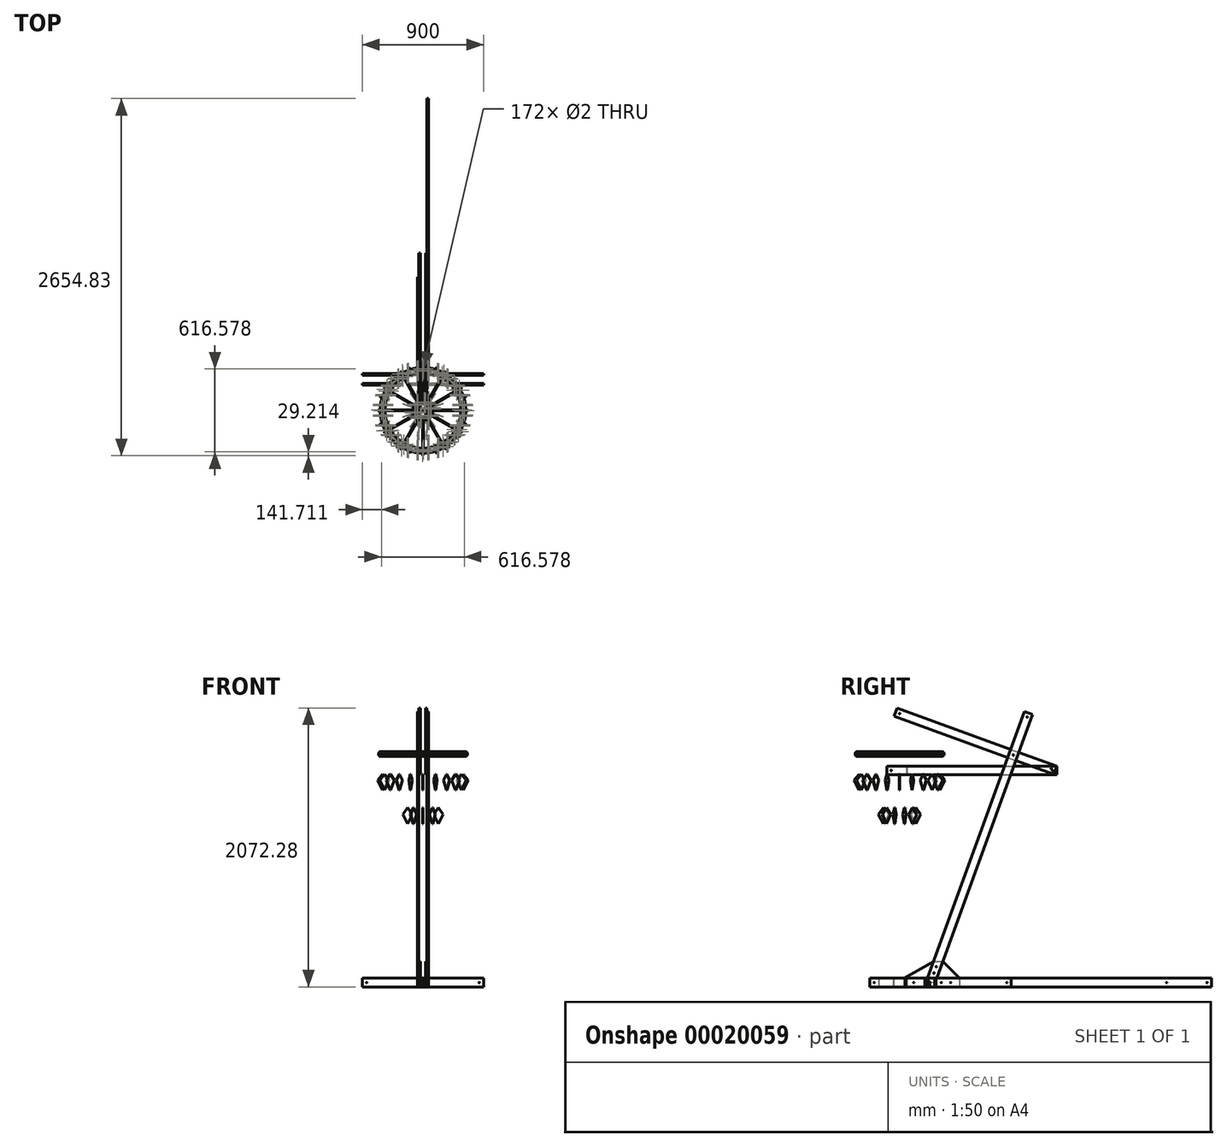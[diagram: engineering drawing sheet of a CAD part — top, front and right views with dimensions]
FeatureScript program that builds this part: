
annotation { "Feature Type Name" : "Feature", "Feature Type Description" : "" }
export const myFeature = defineFeature(function(context is Context, id is Id, definition is map)
    precondition{}
    {
        {
            var Q0;
            Q0=qCreatedBy(makeId("Right.planeOp"),FACE);
            var sketch = newSketch(context, id + "F0", { "sketchPlane" : qUnion([Q0])});
            skLineSegment(sketch, "E0", {"start": v(0, 0) * mm, "end": v(-450, 0) * mm});
            skLineSegment(sketch, "E1", {"start": v(0, 0) * mm, "end": v(600, 0) * mm});
            skLineSegment(sketch, "E2", {"start": v(0, 0) * mm, "end": v(615.64, 1691.45) * mm});
            skLineSegment(sketch, "E3", {"start": v(615.64, 1691.45) * mm, "end": v(718.24, 1973.35) * mm});
            skLineSegment(sketch, "E4", {"start": v(615.64, 1691.45) * mm, "end": v(897.54, 1588.84) * mm});
            skLineSegment(sketch, "E5", {"start": v(615.64, 1691.45) * mm, "end": v(-230.09, 1999.26) * mm});
            skLineSegment(sketch, "E6", {"start": v(-230.09, 1999.26) * mm, "end": v(-230.09, 1699.26) * mm});
            skLineSegment(sketch, "E7", {"start": v(-230.09, 1699.26) * mm, "end": v(-530.09, 1699.26) * mm});
            skLineSegment(sketch, "E8", {"start": v(-230.09, 1699.26) * mm, "end": v(69.91, 1699.26) * mm});
            skLineSegment(sketch, "E9", {"start": v(-530.09, 1699.26) * mm, "end": v(-530.09, 1399.26) * mm});
            skLineSegment(sketch, "E10", {"start": v(69.91, 1699.26) * mm, "end": v(69.91, 1399.26) * mm});
            skSolve(sketch);
        }
        {
            var Q0;
            Q0=qCreatedBy(makeId("Front.planeOp"),FACE);
            var sketch = newSketch(context, id + "F1", { "sketchPlane" : qUnion([Q0])});
            skLineSegment(sketch, "E11", {"start": v(0, 0) * mm, "end": v(450, 0) * mm});
            skLineSegment(sketch, "E12", {"start": v(0, 0) * mm, "end": v(-450, 0) * mm});
            skSolve(sketch);
        }
        {
            var Q0;
            Q0=qCreatedBy(makeId("Right.planeOp"),FACE);
            var sketch = newSketch(context, id + "F2", { "sketchPlane" : qUnion([Q0])});
            skLineSegment(sketch, "E13.0", {"start": v(-230.09, 1699.26) * mm, "end": v(69.91, 1699.26) * mm});
            skLineSegment(sketch, "E14", {"start": v(-230.09, 1693.26) * mm, "end": v(69.91, 1693.26) * mm});
            skLineSegment(sketch, "E15", {"start": v(69.91, 1693.26) * mm, "end": v(69.91, 1699.26) * mm});
            skLineSegment(sketch, "E16", {"start": v(-230.09, 1699.26) * mm, "end": v(-230.09, 1693.26) * mm});
            skSolve(sketch);
        }
        {
            var Q0;
            Q0=makeQuery(id+"F2.imprint","IMPRINT",FACE,{"disambiguationData":[TD([[makeQuery(id+"F2.imprint","IMPRINT",EDGE,{"derivedFrom":sQuery(id+"F2.wireOp",EDGE,"E13.0")}),-1.0]])]});
            var Q1;
            Q1=sQuery(id+"F0.wireOp",EDGE,"E6");
            revolve(context, id + "F3", {"entities" : qUnion([Q0]), "axis" : qUnion([Q1]), "revolveType" : RevolveType.FULL});
        }
        {
            var Q0;
            Q0=qCreatedBy(makeId("Right.planeOp"),FACE);
            var sketch = newSketch(context, id + "F4", { "sketchPlane" : qUnion([Q0])});
            skLineSegment(sketch, "E17", {"start": v(-450.4, 0) * mm, "end": v(-450.4, 32) * mm});
            skPoint(sketch, "E18.0", {"position": v(600, 0) * mm});
            skLineSegment(sketch, "E19", {"start": v(-450.4, 32) * mm, "end": v(-42, 32) * mm});
            skLineSegment(sketch, "E20", {"start": v(600, 32) * mm, "end": v(600, 0) * mm});
            skLineSegment(sketch, "E21", {"start": v(600, 0) * mm, "end": v(600, -32) * mm});
            skLineSegment(sketch, "E22", {"start": v(600, -32) * mm, "end": v(-450.4, -32) * mm});
            skLineSegment(sketch, "E23", {"start": v(-450.4, -32) * mm, "end": v(-450.4, 0) * mm});
            skLineSegment(sketch, "E24.top", {"start": v(-30, 0) * mm, "end": v(-42, 0) * mm});
            skLineSegment(sketch, "E24.left", {"start": v(-30, 32) * mm, "end": v(-30, 0) * mm});
            skLineSegment(sketch, "E24.right", {"start": v(-42, 32) * mm, "end": v(-42, 0) * mm});
            skLineSegment(sketch, "E25.top", {"start": v(30, 0) * mm, "end": v(42, 0) * mm});
            skLineSegment(sketch, "E25.left", {"start": v(30, 32) * mm, "end": v(30, 0) * mm});
            skLineSegment(sketch, "E25.right", {"start": v(42, 32) * mm, "end": v(42, 0) * mm});
            skLineSegment(sketch, "E26.trimOffspring", {"start": v(-30, 32) * mm, "end": v(30, 32) * mm});
            skLineSegment(sketch, "E27.trimOffspring", {"start": v(42, 32) * mm, "end": v(600, 32) * mm});
            skLineSegment(sketch, "E28", {"start": v(0, 0) * mm, "end": v(0, 32) * mm, "construction": true});
            skSolve(sketch);
        }
        {
            var Q0;
            Q0=makeQuery(id+"F4.imprint","IMPRINT",FACE,{"disambiguationData":[TD([[makeQuery(id+"F4.imprint","IMPRINT",EDGE,{"derivedFrom":sQuery(id+"F4.wireOp",EDGE,"E17")}),-1.0]])]});
            extrude(context, id + "F5", {"entities" : qUnion([Q0]), "depth" : 12 * mm});
        }
        {
            var Q0;
            Q0=makeQuery(id+"F5.opExtrude","SWEPT_BODY",BODY,{"disambiguationData":[OSD([sQuery(id+"F4.wireOp",EDGE,"E17"),sQuery(id+"F4.wireOp",EDGE,"E19"),sQuery(id+"F4.wireOp",EDGE,"E20"),sQuery(id+"F4.wireOp",EDGE,"E21"),sQuery(id+"F4.wireOp",EDGE,"E22"),sQuery(id+"F4.wireOp",EDGE,"E23")])]});
            var Q1;
            Q1=sQuery(id+"F1.wireOp",EDGE,"E11");
            transform(context, id + "F6", {"entities" : qUnion([Q0]), "transformType" : TransformType.TRANSLATION_DISTANCE, "transformDirection" : qUnion([Q1]), "distance" : (12 * 2.5) * mm, "makeCopy" : false});
        }
        {
            var Q0;
            Q0=makeQuery(id+"F5.opExtrude","SWEPT_BODY",BODY,{"disambiguationData":[OSD([sQuery(id+"F4.wireOp",EDGE,"E17"),sQuery(id+"F4.wireOp",EDGE,"E19"),sQuery(id+"F4.wireOp",EDGE,"E20"),sQuery(id+"F4.wireOp",EDGE,"E21"),sQuery(id+"F4.wireOp",EDGE,"E22"),sQuery(id+"F4.wireOp",EDGE,"E23")])]});
            var Q1;
            Q1=qCreatedBy(makeId("Right.planeOp"),FACE);
            mirror(context, id + "F7", {"entities" : qUnion([Q0]), "mirrorPlane" : qUnion([Q1])});
        }
        {
            var Q0;
            Q0=qCreatedBy(makeId("Front.planeOp"),FACE);
            var sketch = newSketch(context, id + "F8", { "sketchPlane" : qUnion([Q0])});
            skPoint(sketch, "E29.0", {"position": v(-450, 0) * mm});
            skPoint(sketch, "E30.0", {"position": v(450, 0) * mm});
            skLineSegment(sketch, "E31", {"start": v(-450, 0) * mm, "end": v(-450, 32) * mm});
            skLineSegment(sketch, "E32", {"start": v(450, 32) * mm, "end": v(450, 0) * mm});
            skLineSegment(sketch, "E33", {"start": v(450, 0) * mm, "end": v(450, -32) * mm});
            skLineSegment(sketch, "E34", {"start": v(450, -32) * mm, "end": v(42, -32) * mm});
            skLineSegment(sketch, "E35", {"start": v(-450, -32) * mm, "end": v(-450, 0) * mm});
            skLineSegment(sketch, "E36.0.0", {"start": v(30, 32) * mm, "end": v(30, -32) * mm, "construction": true});
            skLineSegment(sketch, "E36.0.1", {"start": v(30, -32) * mm, "end": v(42, -32) * mm, "construction": true});
            skLineSegment(sketch, "E36.0.2", {"start": v(42, -32) * mm, "end": v(42, 32) * mm, "construction": true});
            skLineSegment(sketch, "E36.0.3", {"start": v(42, 32) * mm, "end": v(30, 32) * mm, "construction": true});
            skLineSegment(sketch, "E37.0.0", {"start": v(-30, -32) * mm, "end": v(-30, 32) * mm, "construction": true});
            skLineSegment(sketch, "E37.0.1", {"start": v(-30, 32) * mm, "end": v(-42, 32) * mm, "construction": true});
            skLineSegment(sketch, "E37.0.2", {"start": v(-42, 32) * mm, "end": v(-42, -32) * mm, "construction": true});
            skLineSegment(sketch, "E37.0.3", {"start": v(-42, -32) * mm, "end": v(-30, -32) * mm, "construction": true});
            skLineSegment(sketch, "E38", {"start": v(-42, 0) * mm, "end": v(-30, 0) * mm});
            skLineSegment(sketch, "E39", {"start": v(-450, 32) * mm, "end": v(450, 32) * mm});
            skLineSegment(sketch, "E40", {"start": v(-42, -32) * mm, "end": v(-42, 0) * mm});
            skLineSegment(sketch, "E41", {"start": v(-30, 0) * mm, "end": v(-30, -32) * mm});
            skLineSegment(sketch, "E42", {"start": v(30, -32) * mm, "end": v(30, 0) * mm});
            skLineSegment(sketch, "E43", {"start": v(30, 0) * mm, "end": v(42, 0) * mm});
            skLineSegment(sketch, "E44", {"start": v(42, 0) * mm, "end": v(42, -32) * mm});
            skLineSegment(sketch, "E45.trimOffspring", {"start": v(-42, -32) * mm, "end": v(-450, -32) * mm});
            skLineSegment(sketch, "E46.trimOffspring", {"start": v(30, -32) * mm, "end": v(-30, -32) * mm});
            skLineSegment(sketch, "E47.0", {"start": v(-42, 32) * mm, "end": v(-30, 32) * mm, "construction": true});
            skSolve(sketch);
        }
        {
            var Q0;
            Q0=makeQuery(id+"F8.imprint","IMPRINT",FACE,{"disambiguationData":[TD([[makeQuery(id+"F8.imprint","IMPRINT",EDGE,{"derivedFrom":sQuery(id+"F8.wireOp",EDGE,"E31")}),-1.0]])]});
            extrude(context, id + "F9", {"entities" : qUnion([Q0]), "depth" : 12 * mm});
        }
        {
            var Q0;
            Q0=makeQuery(id+"F9.opExtrude","SWEPT_BODY",BODY,{"disambiguationData":[OSD([sQuery(id+"F8.wireOp",EDGE,"E31"),sQuery(id+"F8.wireOp",EDGE,"6637da51-7d9f-46c2-a1c9-c0c26d9a3ec1"),sQuery(id+"F8.wireOp",EDGE,"E32"),sQuery(id+"F8.wireOp",EDGE,"E33"),sQuery(id+"F8.wireOp",EDGE,"E34"),sQuery(id+"F8.wireOp",EDGE,"E35")])]});
            var Q1;
            Q1=sQuery(id+"F0.wireOp",EDGE,"E0");
            transform(context, id + "F10", {"entities" : qUnion([Q0]), "transformType" : TransformType.TRANSLATION_DISTANCE, "transformDirection" : qUnion([Q1]), "distance" : 30 * mm, "makeCopy" : false});
        }
        {
            var Q0;
            Q0=makeQuery(id+"F9.opExtrude","SWEPT_BODY",BODY,{"disambiguationData":[OSD([sQuery(id+"F8.wireOp",EDGE,"E31"),sQuery(id+"F8.wireOp",EDGE,"6637da51-7d9f-46c2-a1c9-c0c26d9a3ec1"),sQuery(id+"F8.wireOp",EDGE,"E32"),sQuery(id+"F8.wireOp",EDGE,"E33"),sQuery(id+"F8.wireOp",EDGE,"E34"),sQuery(id+"F8.wireOp",EDGE,"E35")])]});
            var Q1;
            Q1=qCreatedBy(makeId("Front.planeOp"),FACE);
            mirror(context, id + "F11", {"entities" : qUnion([Q0]), "mirrorPlane" : qUnion([Q1])});
        }
        {
            var Q0;
            Q0=qCreatedBy(makeId("Right.planeOp"),FACE);
            var sketch = newSketch(context, id + "F12", { "sketchPlane" : qUnion([Q0])});
            skLineSegment(sketch, "E48.0", {"start": v(0, 0) * mm, "end": v(615.64, 1691.45) * mm, "construction": true});
            skLineSegment(sketch, "E49.0", {"start": v(615.64, 1691.45) * mm, "end": v(718.24, 1973.35) * mm, "construction": true});
            skLineSegment(sketch, "E50", {"start": v(718.24, 1973.35) * mm, "end": v(688.25, 1984.27) * mm});
            skLineSegment(sketch, "E51", {"start": v(688.25, 1984.27) * mm, "end": v(-22.32, 32) * mm});
            skLineSegment(sketch, "E52", {"start": v(718.24, 1973.35) * mm, "end": v(748.39, 1962.38) * mm});
            skLineSegment(sketch, "E53", {"start": v(748.39, 1962.38) * mm, "end": v(45.78, 32) * mm});
            skLineSegment(sketch, "E54.0", {"start": v(-450.4, 32) * mm, "end": v(-450.4, 32) * mm});
            skLineSegment(sketch, "E55", {"start": v(-22.32, 32) * mm, "end": v(45.78, 32) * mm});
            skSolve(sketch);
        }
        {
            var Q0;
            Q0=makeQuery(id+"F12.imprint","IMPRINT",FACE,{"disambiguationData":[TD([[makeQuery(id+"F12.imprint","IMPRINT",EDGE,{"derivedFrom":sQuery(id+"F12.wireOp",EDGE,"E50")}),1.0]])]});
            extrude(context, id + "F13", {"entities" : qUnion([Q0]), "depth" : 12 * mm});
        }
        {
            var Q0;
            Q0=makeQuery(id+"F13.opExtrude","SWEPT_BODY",BODY,{"disambiguationData":[OSD([sQuery(id+"F12.wireOp",EDGE,"E50"),sQuery(id+"F12.wireOp",EDGE,"E51"),sQuery(id+"F12.wireOp",EDGE,"E52"),sQuery(id+"F12.wireOp",EDGE,"E53"),sQuery(id+"F12.wireOp",EDGE,"E55")])]});
            var Q1;
            Q1=sQuery(id+"F1.wireOp",EDGE,"E11");
            transform(context, id + "F14", {"entities" : qUnion([Q0]), "transformType" : TransformType.TRANSLATION_DISTANCE, "transformDirection" : qUnion([Q1]), "distance" : 30 * mm, "makeCopy" : false});
        }
        {
            var Q0;
            Q0=makeQuery(id+"F13.opExtrude","SWEPT_BODY",BODY,{"disambiguationData":[OSD([sQuery(id+"F12.wireOp",EDGE,"E50"),sQuery(id+"F12.wireOp",EDGE,"E51"),sQuery(id+"F12.wireOp",EDGE,"E52"),sQuery(id+"F12.wireOp",EDGE,"E53"),sQuery(id+"F12.wireOp",EDGE,"E55")])]});
            var Q1;
            Q1=qCreatedBy(makeId("Right.planeOp"),FACE);
            mirror(context, id + "F15", {"entities" : qUnion([Q0]), "mirrorPlane" : qUnion([Q1])});
        }
        {
            var Q0;
            Q0=qCreatedBy(makeId("Right.planeOp"),FACE);
            var sketch = newSketch(context, id + "F16", { "sketchPlane" : qUnion([Q0])});
            skLineSegment(sketch, "E56.0", {"start": v(615.64, 1691.45) * mm, "end": v(-230.09, 1999.26) * mm, "construction": true});
            skLineSegment(sketch, "E57.0", {"start": v(615.64, 1691.45) * mm, "end": v(897.54, 1588.84) * mm, "construction": true});
            skLineSegment(sketch, "E58", {"start": v(-230.09, 1999.26) * mm, "end": v(-219.14, 2029.34) * mm});
            skLineSegment(sketch, "E59", {"start": v(897.54, 1588.84) * mm, "end": v(908.49, 1618.91) * mm});
            skLineSegment(sketch, "E60", {"start": v(897.54, 1588.84) * mm, "end": v(886.6, 1558.77) * mm});
            skLineSegment(sketch, "E61", {"start": v(-230.09, 1999.26) * mm, "end": v(-241.03, 1969.2) * mm});
            skLineSegment(sketch, "E62", {"start": v(-219.14, 2029.34) * mm, "end": v(908.49, 1618.91) * mm});
            skLineSegment(sketch, "E63", {"start": v(-241.03, 1969.2) * mm, "end": v(886.6, 1558.77) * mm});
            skSolve(sketch);
        }
        {
            var Q0;
            Q0=makeQuery(id+"F16.imprint","IMPRINT",FACE,{"disambiguationData":[TD([[makeQuery(id+"F16.imprint","IMPRINT",EDGE,{"derivedFrom":sQuery(id+"F16.wireOp",EDGE,"E58")}),-1.0]])]});
            extrude(context, id + "F17", {"entities" : qUnion([Q0]), "depth" : 12 * mm});
        }
        {
            var Q0;
            Q0=makeQuery(id+"F17.opExtrude","SWEPT_BODY",BODY,{"disambiguationData":[OSD([sQuery(id+"F16.wireOp",EDGE,"E58"),sQuery(id+"F16.wireOp",EDGE,"E59"),sQuery(id+"F16.wireOp",EDGE,"E60"),sQuery(id+"F16.wireOp",EDGE,"E61"),sQuery(id+"F16.wireOp",EDGE,"E62"),sQuery(id+"F16.wireOp",EDGE,"E63")])]});
            var Q1;
            Q1=sQuery(id+"F1.wireOp",EDGE,"E11");
            transform(context, id + "F18", {"entities" : qUnion([Q0]), "transformType" : TransformType.TRANSLATION_DISTANCE, "transformDirection" : qUnion([Q1]), "distance" : (30 - 12) * mm, "makeCopy" : false});
        }
        {
            var Q0;
            Q0=makeQuery(id+"F17.opExtrude","SWEPT_BODY",BODY,{"disambiguationData":[OSD([sQuery(id+"F16.wireOp",EDGE,"E58"),sQuery(id+"F16.wireOp",EDGE,"E59"),sQuery(id+"F16.wireOp",EDGE,"E60"),sQuery(id+"F16.wireOp",EDGE,"E61"),sQuery(id+"F16.wireOp",EDGE,"E62"),sQuery(id+"F16.wireOp",EDGE,"E63")])]});
            var Q1;
            Q1=qCreatedBy(makeId("Right.planeOp"),FACE);
            mirror(context, id + "F19", {"entities" : qUnion([Q0]), "mirrorPlane" : qUnion([Q1])});
        }
        {
            var Q0;
            Q0=qCreatedBy(makeId("Right.planeOp"),FACE);
            var sketch = newSketch(context, id + "F20", { "sketchPlane" : qUnion([Q0])});
            skLineSegment(sketch, "E64.0", {"start": v(-450.4, 32) * mm, "end": v(-450.4, 32) * mm});
            skLineSegment(sketch, "E65.0", {"start": v(600, -32) * mm, "end": v(-450.4, -32) * mm, "construction": true});
            skLineSegment(sketch, "E66.0", {"start": v(-42, 32) * mm, "end": v(-42, -32) * mm, "construction": true});
            skLineSegment(sketch, "E67.0.0", {"start": v(-450.4, 32) * mm, "end": v(-450.4, -32) * mm, "construction": true});
            skLineSegment(sketch, "E67.0.1", {"start": v(-450.4, -32) * mm, "end": v(600, -32) * mm, "construction": true});
            skLineSegment(sketch, "E68.0", {"start": v(-30, 32) * mm, "end": v(-30, -32) * mm, "construction": true});
            skLineSegment(sketch, "E69.0", {"start": v(30, 32) * mm, "end": v(30, -32) * mm, "construction": true});
            skLineSegment(sketch, "E70.0", {"start": v(42, 32) * mm, "end": v(42, -32) * mm, "construction": true});
            skLineSegment(sketch, "E71.0", {"start": v(688.25, 1984.27) * mm, "end": v(-22.32, 32) * mm, "construction": true});
            skLineSegment(sketch, "E72.0", {"start": v(748.39, 1962.38) * mm, "end": v(45.78, 32) * mm, "construction": true});
            skLineSegment(sketch, "E73", {"start": v(-193.33, -32) * mm, "end": v(-193.33, 32) * mm});
            skLineSegment(sketch, "E74", {"start": v(-193.33, 32) * mm, "end": v(23.17, 157) * mm});
            skLineSegment(sketch, "E75", {"start": v(23.17, 157) * mm, "end": v(91.28, 157) * mm});
            skLineSegment(sketch, "E76", {"start": v(91.28, 157) * mm, "end": v(216.28, 32) * mm});
            skLineSegment(sketch, "E77", {"start": v(216.28, 32) * mm, "end": v(216.28, -32) * mm});
            skLineSegment(sketch, "E78", {"start": v(216.28, -32) * mm, "end": v(42, -32) * mm});
            skLineSegment(sketch, "E79", {"start": v(42, -32) * mm, "end": v(42, 32) * mm});
            skLineSegment(sketch, "E80", {"start": v(42, 32) * mm, "end": v(30, 32) * mm});
            skLineSegment(sketch, "E81", {"start": v(30, 32) * mm, "end": v(30, -32) * mm});
            skLineSegment(sketch, "E82", {"start": v(-30, -32) * mm, "end": v(-30, 32) * mm});
            skLineSegment(sketch, "E83", {"start": v(-30, 32) * mm, "end": v(-42, 32) * mm});
            skLineSegment(sketch, "E84", {"start": v(-42, 32) * mm, "end": v(-42, -32) * mm});
            skLineSegment(sketch, "E85", {"start": v(-42, -32) * mm, "end": v(-193.33, -32) * mm});
            skLineSegment(sketch, "E86", {"start": v(-30, -32) * mm, "end": v(30, -32) * mm});
            skSolve(sketch);
        }
        {
            var Q0;
            Q0=makeQuery(id+"F20.imprint","IMPRINT",FACE,{"disambiguationData":[TD([[makeQuery(id+"F20.imprint","IMPRINT",EDGE,{"derivedFrom":sQuery(id+"F20.wireOp",EDGE,"E73")}),-1.0]])]});
            extrude(context, id + "F21", {"entities" : qUnion([Q0]), "depth" : 12 * mm});
        }
        {
            var Q0;
            Q0=makeQuery(id+"F21.opExtrude","SWEPT_BODY",BODY,{"disambiguationData":[OSD([sQuery(id+"F20.wireOp",EDGE,"E73"),sQuery(id+"F20.wireOp",EDGE,"E74"),sQuery(id+"F20.wireOp",EDGE,"E75"),sQuery(id+"F20.wireOp",EDGE,"E76"),sQuery(id+"F20.wireOp",EDGE,"E77"),sQuery(id+"F20.wireOp",EDGE,"E78"),sQuery(id+"F20.wireOp",EDGE,"E79"),sQuery(id+"F20.wireOp",EDGE,"E80"),sQuery(id+"F20.wireOp",EDGE,"E81"),sQuery(id+"F20.wireOp",EDGE,"E82"),sQuery(id+"F20.wireOp",EDGE,"E83"),sQuery(id+"F20.wireOp",EDGE,"E84"),sQuery(id+"F20.wireOp",EDGE,"E85"),sQuery(id+"F20.wireOp",EDGE,"E86")])]});
            var Q1;
            Q1=sQuery(id+"F1.wireOp",EDGE,"E11");
            transform(context, id + "F22", {"entities" : qUnion([Q0]), "transformType" : TransformType.TRANSLATION_DISTANCE, "transformDirection" : qUnion([Q1]), "distance" : 18 * mm, "makeCopy" : false});
        }
        {
            var Q0;
            Q0=makeQuery(id+"F21.opExtrude","SWEPT_BODY",BODY,{"disambiguationData":[OSD([sQuery(id+"F20.wireOp",EDGE,"E73"),sQuery(id+"F20.wireOp",EDGE,"E74"),sQuery(id+"F20.wireOp",EDGE,"E75"),sQuery(id+"F20.wireOp",EDGE,"E76"),sQuery(id+"F20.wireOp",EDGE,"E77"),sQuery(id+"F20.wireOp",EDGE,"E78"),sQuery(id+"F20.wireOp",EDGE,"E79"),sQuery(id+"F20.wireOp",EDGE,"E80"),sQuery(id+"F20.wireOp",EDGE,"E81"),sQuery(id+"F20.wireOp",EDGE,"E82"),sQuery(id+"F20.wireOp",EDGE,"E83"),sQuery(id+"F20.wireOp",EDGE,"E84"),sQuery(id+"F20.wireOp",EDGE,"E85"),sQuery(id+"F20.wireOp",EDGE,"E86")])]});
            var Q1;
            Q1=qCreatedBy(makeId("Right.planeOp"),FACE);
            mirror(context, id + "F23", {"entities" : qUnion([Q0]), "mirrorPlane" : qUnion([Q1])});
        }
        {
            var Q0;
            Q0=makeQuery(id+"F15.opPattern","COPY",FACE,{"derivedFrom":makeQuery(id+"F13.opExtrude","SWEPT_FACE",FACE,{"disambiguationData":[OSD([sQuery(id+"F12.wireOp",EDGE,"E50"),sQuery(id+"F12.wireOp",EDGE,"E52")])]}),"instanceName":"1"});
            var Q1;
            Q1=makeQuery(id+"F13.opExtrude","SWEPT_FACE",FACE,{"disambiguationData":[OSD([sQuery(id+"F12.wireOp",EDGE,"E50"),sQuery(id+"F12.wireOp",EDGE,"E52")])]});
            extrude(context, id + "F24", {"entities" : qUnion([Q0, Q1]), "operationType" : NewBodyOperationType.ADD, "depth" : 32 * mm});
        }
        {
            var Q0;
            Q0=makeQuery(id+"F17.opExtrude","SWEPT_FACE",FACE,{"disambiguationData":[OSD([sQuery(id+"F16.wireOp",EDGE,"E59"),sQuery(id+"F16.wireOp",EDGE,"E60")])]});
            var Q1;
            Q1=makeQuery(id+"F19.opPattern","COPY",FACE,{"derivedFrom":makeQuery(id+"F17.opExtrude","SWEPT_FACE",FACE,{"disambiguationData":[OSD([sQuery(id+"F16.wireOp",EDGE,"E59"),sQuery(id+"F16.wireOp",EDGE,"E60")])]}),"instanceName":"1"});
            extrude(context, id + "F25", {"entities" : qUnion([Q0, Q1]), "operationType" : NewBodyOperationType.ADD, "depth" : 32 * mm});
        }
        {
            var Q0;
            Q0=makeQuery(id+"F19.opPattern","COPY",FACE,{"derivedFrom":makeQuery(id+"F17.opExtrude","SWEPT_FACE",FACE,{"disambiguationData":[OSD([sQuery(id+"F16.wireOp",EDGE,"E58"),sQuery(id+"F16.wireOp",EDGE,"E61")])]}),"instanceName":"1"});
            var Q1;
            Q1=makeQuery(id+"F17.opExtrude","SWEPT_FACE",FACE,{"disambiguationData":[OSD([sQuery(id+"F16.wireOp",EDGE,"E58"),sQuery(id+"F16.wireOp",EDGE,"E61")])]});
            extrude(context, id + "F26", {"entities" : qUnion([Q0, Q1]), "operationType" : NewBodyOperationType.ADD, "depth" : 32 * mm});
        }
        {
            var Q0;
            Q0=qCreatedBy(makeId("Right.planeOp"),FACE);
            var sketch = newSketch(context, id + "F27", { "sketchPlane" : qUnion([Q0])});
            skPoint(sketch, "E87.0", {"position": v(-530.09, 1699.26) * mm});
            skPoint(sketch, "E88.0", {"position": v(69.91, 1699.26) * mm});
            skPoint(sketch, "E89.0", {"position": v(-230.09, 1999.26) * mm});
            skPoint(sketch, "E90.0", {"position": v(718.24, 1973.35) * mm});
            skPoint(sketch, "E91.0", {"position": v(897.54, 1588.84) * mm});
            skPoint(sketch, "E92.0", {"position": v(0, 0) * mm});
            skLineSegment(sketch, "E93", {"start": v(718.24, 1973.35) * mm, "end": v(897.54, 1588.84) * mm, "construction": true});
            skLineSegment(sketch, "E94", {"start": v(897.54, 1588.84) * mm, "end": v(0, 0) * mm, "construction": true});
            skCircle(sketch, "E95", {"center": v(718.24, 1973.35) * mm, "radius": 18 * mm, "construction": true});
            skCircle(sketch, "E96", {"center": v(897.54, 1588.84) * mm, "radius": 18 * mm, "construction": true});
            skLineSegment(sketch, "E97", {"start": v(-230.09, 1999.26) * mm, "end": v(718.42, 1987.85) * mm});
            skLineSegment(sketch, "E98", {"start": v(731.38, 1979.48) * mm, "end": v(910.69, 1594.97) * mm});
            skArc(sketch, "E99", {"start": v(718.42, 1987.85) * mm, "mid": v(710.38, 1961.17) * mm, "end": v(731.38, 1979.48) * mm, "construction": true});
            skArc(sketch, "E100", {"start": v(731.38, 1979.48) * mm, "mid": v(726.1, 1985.54) * mm, "end": v(718.42, 1987.85) * mm});
            skLineSegment(sketch, "E101", {"start": v(0, 0) * mm, "end": v(910.11, 1581.6) * mm});
            skArc(sketch, "E102", {"start": v(910.11, 1581.6) * mm, "mid": v(912.03, 1588.22) * mm, "end": v(910.69, 1594.97) * mm});
            skArc(sketch, "E103", {"start": v(910.69, 1594.97) * mm, "mid": v(883.06, 1589.46) * mm, "end": v(910.11, 1581.6) * mm, "construction": true});
            skLineSegment(sketch, "E104", {"start": v(-230.09, 1999.26) * mm, "end": v(-230.09, 1699.44) * mm});
            skSolve(sketch);
        }
        {
            var Q0;
            Q0=qCreatedBy(makeId("Right.planeOp"),FACE);
            var sketch = newSketch(context, id + "F28", { "sketchPlane" : qUnion([Q0])});
            skCircle(sketch, "E105", {"center": v(0, 0) * mm, "radius": 3 * mm});
            skPoint(sketch, "E106.0", {"position": v(897.54, 1588.84) * mm});
            skCircle(sketch, "E107", {"center": v(897.54, 1588.84) * mm, "radius": 3 * mm});
            skPoint(sketch, "E108.0", {"position": v(718.24, 1973.35) * mm});
            skCircle(sketch, "E109", {"center": v(718.24, 1973.35) * mm, "radius": 3 * mm});
            skPoint(sketch, "E110.0", {"position": v(-230.09, 1999.26) * mm});
            skCircle(sketch, "E111", {"center": v(-230.09, 1999.26) * mm, "radius": 3 * mm});
            skCircle(sketch, "E112", {"center": v(-418.4, 0) * mm, "radius": 3 * mm});
            skCircle(sketch, "E113", {"center": v(150, 0) * mm, "radius": 3 * mm});
            skCircle(sketch, "E114", {"center": v(-125, 0) * mm, "radius": 3 * mm});
            skCircle(sketch, "E115", {"center": v(568, 0) * mm, "radius": 3 * mm});
            skPoint(sketch, "E116.0", {"position": v(615.64, 1691.45) * mm});
            skCircle(sketch, "E117", {"center": v(615.64, 1691.45) * mm, "radius": 3 * mm});
            skLineSegment(sketch, "E118.0", {"start": v(0, 0) * mm, "end": v(615.64, 1691.45) * mm, "construction": true});
            skCircle(sketch, "E119", {"center": v(42.75, 117.46) * mm, "radius": 3 * mm});
            skCircle(sketch, "E120", {"center": v(25.65, 70.48) * mm, "radius": 3 * mm});
            skSolve(sketch);
        }
        {
            var Q0;
            Q0 = qSketchRegion(id + "F28", true);
            extrude(context, id + "F29", {"entities" : qUnion([Q0]), "operationType" : NewBodyOperationType.REMOVE, "endBound" : BoundingType.THROUGH_ALL, "depth" : 25 * mm, "hasSecondDirection" : true, "secondDirectionBound" : SecondDirectionBoundingType.THROUGH_ALL, "secondDirectionOppositeDirection" : true, "secondDirectionDepth" : 25 * mm});
        }
        {
            var Q0;
            Q0=qCreatedBy(makeId("Front.planeOp"),FACE);
            var sketch = newSketch(context, id + "F30", { "sketchPlane" : qUnion([Q0])});
            skCircle(sketch, "E121", {"center": v(-418, 0) * mm, "radius": 3 * mm});
            skCircle(sketch, "E122", {"center": v(418, 0) * mm, "radius": 3 * mm});
            skSolve(sketch);
        }
        {
            var Q0;
            Q0 = qSketchRegion(id + "F30", true);
            extrude(context, id + "F31", {"entities" : qUnion([Q0]), "operationType" : NewBodyOperationType.REMOVE, "endBound" : BoundingType.THROUGH_ALL, "oppositeDirection" : true, "depth" : 25 * mm, "hasSecondDirection" : true, "secondDirectionBound" : SecondDirectionBoundingType.THROUGH_ALL, "secondDirectionOppositeDirection" : false, "secondDirectionDepth" : 25 * mm});
        }
        {
            var Q0;
            Q0=qCreatedBy(makeId("Right.planeOp"),FACE);
            var sketch = newSketch(context, id + "F32", { "sketchPlane" : qUnion([Q0])});
            skLineSegment(sketch, "E123.0", {"start": v(-450.4, 32) * mm, "end": v(-42, 32) * mm, "construction": true});
            skLineSegment(sketch, "E124.0", {"start": v(600, -32) * mm, "end": v(-450.4, -32) * mm, "construction": true});
            skLineSegment(sketch, "E125.bottom", {"start": v(-450.4, 32) * mm, "end": v(-386.4, 32) * mm});
            skLineSegment(sketch, "E125.top", {"start": v(-450.4, -32) * mm, "end": v(-386.4, -32) * mm});
            skLineSegment(sketch, "E125.left", {"start": v(-450.4, 32) * mm, "end": v(-450.4, -32) * mm});
            skLineSegment(sketch, "E125.right", {"start": v(-386.4, 32) * mm, "end": v(-386.4, -32) * mm});
            skCircle(sketch, "E126.0", {"center": v(-418.4, 0) * mm, "radius": 3 * mm});
            skSolve(sketch);
        }
        {
            var Q0;
            Q0=makeQuery(id+"F32.imprint","IMPRINT",FACE,{"disambiguationData":[TD([[makeQuery(id+"F32.imprint","IMPRINT",EDGE,{"derivedFrom":sQuery(id+"F32.wireOp",EDGE,"E125.bottom")}),-1.0]])]});
            extrude(context, id + "F33", {"entities" : qUnion([Q0]), "depth" : 12 * mm});
        }
        {
            var Q0;
            Q0=qCreatedBy(makeId("Right.planeOp"),FACE);
            var sketch = newSketch(context, id + "F34", { "sketchPlane" : qUnion([Q0])});
            skPoint(sketch, "E127.0", {"position": v(69.91, 1699.26) * mm});
            skLineSegment(sketch, "E128", {"start": v(69.91, 1699.26) * mm, "end": v(69.91, 1549.26) * mm, "construction": true});
            skLineSegment(sketch, "E129", {"start": v(69.91, 1549.26) * mm, "end": v(32.41, 1504.74) * mm});
            skLineSegment(sketch, "E130", {"start": v(32.41, 1504.74) * mm, "end": v(69.91, 1429.26) * mm});
            skLineSegment(sketch, "E131", {"start": v(69.91, 1429.26) * mm, "end": v(107.41, 1504.74) * mm});
            skLineSegment(sketch, "E132", {"start": v(107.41, 1504.74) * mm, "end": v(69.91, 1549.26) * mm});
            skSolve(sketch);
        }
        {
            var Q0;
            Q0=makeQuery(id+"F34.imprint","IMPRINT",FACE,{"disambiguationData":[TD([[makeQuery(id+"F34.imprint","IMPRINT",EDGE,{"derivedFrom":sQuery(id+"F34.wireOp",EDGE,"E129")}),1.0]])]});
            extrude(context, id + "F35", {"entities" : qUnion([Q0]), "endBound" : BoundingType.SYMMETRIC, "depth" : 3 * mm});
        }
        {
            var Q0;
            Q0=makeQuery(id+"F35.opExtrude","SWEPT_BODY",BODY,{"disambiguationData":[OSD([sQuery(id+"F34.wireOp",EDGE,"E129"),sQuery(id+"F34.wireOp",EDGE,"E130"),sQuery(id+"F34.wireOp",EDGE,"E131"),sQuery(id+"F34.wireOp",EDGE,"E132")])]});
            var Q1;
            Q1=sQuery(id+"F0.wireOp",EDGE,"E6");
            circularPattern(context, id + "F36", {"entities" : qUnion([Q0]), "axis" : qUnion([Q1]), "angle" : 360 * degree, "instanceCount" : 20, "equalSpace" : true});
        }
        {
            var Q0;
            Q0=qCreatedBy(makeId("Right.planeOp"),FACE);
            var sketch = newSketch(context, id + "F37", { "sketchPlane" : qUnion([Q0])});
            skLineSegment(sketch, "E133.0", {"start": v(-230.09, 1999.26) * mm, "end": v(-230.09, 1699.26) * mm, "construction": true});
            skLineSegment(sketch, "E134.0", {"start": v(-230.09, 1699.26) * mm, "end": v(69.91, 1699.26) * mm, "construction": true});
            skLineSegment(sketch, "E135", {"start": v(-230.09, 1699.26) * mm, "end": v(-110.09, 1699.26) * mm, "construction": true});
            skLineSegment(sketch, "E136", {"start": v(-110.09, 1699.26) * mm, "end": v(-110.09, 1299.26) * mm, "construction": true});
            skLineSegment(sketch, "E137", {"start": v(-110.09, 1299.26) * mm, "end": v(-147.59, 1248.75) * mm});
            skLineSegment(sketch, "E138", {"start": v(-147.59, 1248.75) * mm, "end": v(-110.09, 1179.26) * mm});
            skLineSegment(sketch, "E139", {"start": v(-110.09, 1179.26) * mm, "end": v(-72.59, 1248.75) * mm});
            skLineSegment(sketch, "E140", {"start": v(-72.59, 1248.75) * mm, "end": v(-110.09, 1299.26) * mm});
            skLineSegment(sketch, "E141", {"start": v(-110.09, 1299.26) * mm, "end": v(-110.09, 1179.26) * mm, "construction": true});
            skSolve(sketch);
        }
        {
            var Q0;
            Q0=makeQuery(id+"F37.imprint","IMPRINT",FACE,{"disambiguationData":[TD([[makeQuery(id+"F37.imprint","IMPRINT",EDGE,{"derivedFrom":sQuery(id+"F37.wireOp",EDGE,"E137")}),1.0]])]});
            extrude(context, id + "F38", {"entities" : qUnion([Q0]), "endBound" : BoundingType.SYMMETRIC, "depth" : 3 * mm});
        }
        {
            var Q0;
            Q0=makeQuery(id+"F38.opExtrude","SWEPT_BODY",BODY,{"disambiguationData":[OSD([sQuery(id+"F37.wireOp",EDGE,"E137"),sQuery(id+"F37.wireOp",EDGE,"E138"),sQuery(id+"F37.wireOp",EDGE,"E139"),sQuery(id+"F37.wireOp",EDGE,"E140")])]});
            var Q1;
            Q1=sQuery(id+"F0.wireOp",EDGE,"E6");
            circularPattern(context, id + "F39", {"entities" : qUnion([Q0]), "axis" : qUnion([Q1]), "angle" : 360 * degree, "instanceCount" : 10, "equalSpace" : true});
        }
        {
            var Q0;
            Q0=makeQuery(id+"F13.opExtrude","SWEPT_BODY",BODY,{"disambiguationData":[OSD([sQuery(id+"F12.wireOp",EDGE,"E50"),sQuery(id+"F12.wireOp",EDGE,"E51"),sQuery(id+"F12.wireOp",EDGE,"E52"),sQuery(id+"F12.wireOp",EDGE,"E53"),sQuery(id+"F12.wireOp",EDGE,"E55")])]});
            var Q1;
            Q1=makeQuery(id+"F13.opExtrude","SWEPT_EDGE",EDGE,{"disambiguationData":[OSD([sQuery(id+"F12.wireOp",EDGE,"E51"),sQuery(id+"F12.wireOp",EDGE,"E55")])]});
            transform(context, id + "F40", {"entities" : qUnion([Q0]), "transformType" : TransformType.ROTATION, "transformAxis" : qUnion([Q1]), "angle" : 70 * degree, "makeCopy" : true});
        }
        {
            var Q0;
            Q0=makeQuery(id+"F17.opExtrude","SWEPT_BODY",BODY,{"disambiguationData":[OSD([sQuery(id+"F16.wireOp",EDGE,"E58"),sQuery(id+"F16.wireOp",EDGE,"E59"),sQuery(id+"F16.wireOp",EDGE,"E60"),sQuery(id+"F16.wireOp",EDGE,"E61"),sQuery(id+"F16.wireOp",EDGE,"E62"),sQuery(id+"F16.wireOp",EDGE,"E63")])]});
            var Q1;
            {var subQ0=sQuery(id+"F16.wireOp",EDGE,"E59");var subQ1=sQuery(id+"F16.wireOp",EDGE,"E62");Q1=makeQuery(id+"F25.opExtrude","CAP_EDGE",EDGE,{"disambiguationData":[OSD([subQ0,subQ1]),TDD([makeQuery(id+"F17.opExtrude","SWEPT_EDGE",EDGE,{"disambiguationData":[OSD([subQ0,subQ1])]})])],"isStart":false});}
            transform(context, id + "F41", {"entities" : qUnion([Q0]), "transformType" : TransformType.ROTATION, "transformAxis" : qUnion([Q1]), "angle" : 20 * degree, "oppositeDirection" : true, "makeCopy" : true});
        }
        {
            var Q0;
            Q0=makeQuery(id+"F21.opExtrude","CAP_FACE",FACE,{"disambiguationData":[OSD([sQuery(id+"F20.wireOp",EDGE,"E73"),sQuery(id+"F20.wireOp",EDGE,"E74"),sQuery(id+"F20.wireOp",EDGE,"E75"),sQuery(id+"F20.wireOp",EDGE,"E76"),sQuery(id+"F20.wireOp",EDGE,"E77"),sQuery(id+"F20.wireOp",EDGE,"E78"),sQuery(id+"F20.wireOp",EDGE,"E79"),sQuery(id+"F20.wireOp",EDGE,"E80"),sQuery(id+"F20.wireOp",EDGE,"E81"),sQuery(id+"F20.wireOp",EDGE,"E82"),sQuery(id+"F20.wireOp",EDGE,"E83"),sQuery(id+"F20.wireOp",EDGE,"E84"),sQuery(id+"F20.wireOp",EDGE,"E85"),sQuery(id+"F20.wireOp",EDGE,"E86")])],"isStart":false});
            var sketch = newSketch(context, id + "F42", { "sketchPlane" : qUnion([Q0])});
            skLineSegment(sketch, "E142.0", {"start": v(91.28, 157) * mm, "end": v(216.28, 32) * mm});
            skLineSegment(sketch, "E143.0", {"start": v(0, 0) * mm, "end": v(615.64, 1691.45) * mm, "construction": true});
            skLineSegment(sketch, "E144.0", {"start": v(0, 0) * mm, "end": v(600, 0) * mm, "construction": true});
            skLineSegment(sketch, "E145.0", {"start": v(42, 32) * mm, "end": v(600, 32) * mm, "construction": true});
            skLineSegment(sketch, "E146.0", {"start": v(759.33, 1992.45) * mm, "end": v(45.78, 32) * mm, "construction": true});
            skLineSegment(sketch, "E147", {"start": v(91.28, 157) * mm, "end": v(45.78, 32) * mm});
            skLineSegment(sketch, "E148", {"start": v(45.78, 32) * mm, "end": v(216.28, 32) * mm});
            skSolve(sketch);
        }
        {
            var Q0;
            Q0 = qSketchRegion(id + "F42", true);
            extrude(context, id + "F43", {"entities" : qUnion([Q0]), "depth" : 12 * mm});
        }
        {
            var Q0;
            Q0=qCreatedBy(makeId("Top.planeOp"),FACE);
            var Q1;
            Q1=sQuery(id+"F0.wireOp",VERTEX,"E7.start");
            cPlane(context, id + "F44", {"entities" : qUnion([Q0, Q1]), "cplaneType" : CPlaneType.PLANE_POINT, "offset" : 150 * mm, "width" : 150 * mm, "height" : 150 * mm});
        }
        {
            var Q0;
            Q0=qCreatedBy(id+"F44.planeOp",FACE);
            var sketch = newSketch(context, id + "F45", { "sketchPlane" : qUnion([Q0])});
            skPoint(sketch, "E149.0", {"position": v(0, -230.09) * mm});
            skCircle(sketch, "E150", {"center": v(0, -230.09) * mm, "radius": 75 * mm});
            skCircle(sketch, "E151", {"center": v(0, -230.09) * mm, "radius": 3 * mm});
            skSolve(sketch);
        }
        {
            var Q0;
            Q0=makeQuery(id+"F45.imprint","IMPRINT",FACE,{"disambiguationData":[TD([[makeQuery(id+"F45.imprint","IMPRINT",EDGE,{"derivedFrom":sQuery(id+"F45.wireOp",EDGE,"E150")}),1.0]])]});
            extrude(context, id + "F46", {"entities" : qUnion([Q0]), "depth" : (12.5 + 5) * mm, "hasSecondDirection" : true, "secondDirectionOppositeDirection" : false, "secondDirectionDepth" : 12.5 * mm});
        }
        {
            var Q0;
            Q0=makeQuery(id+"F46.opExtrude","SWEPT_BODY",BODY,{"disambiguationData":[OSD([sQuery(id+"F45.wireOp",EDGE,"E150")])]});
            var Q1;
            Q1=sQuery(id+"F0.wireOp",EDGE,"E6");
            transform(context, id + "F47", {"entities" : qUnion([Q0]), "transformType" : TransformType.TRANSLATION_DISTANCE, "transformDirection" : qUnion([Q1]), "distance" : 31 * mm, "makeCopy" : true});
        }
        {
            var Q0;
            Q0=qCreatedBy(makeId("Right.planeOp"),FACE);
            var sketch = newSketch(context, id + "F48", { "sketchPlane" : qUnion([Q0])});
            skLineSegment(sketch, "E152.0.0", {"start": v(-155.09, 1711.76) * mm, "end": v(-305.09, 1711.76) * mm, "construction": true});
            skLineSegment(sketch, "E153.0.0", {"start": v(-305.09, 1685.76) * mm, "end": v(-155.09, 1685.76) * mm, "construction": true});
            skLineSegment(sketch, "E154.0", {"start": v(-230.09, 1699.26) * mm, "end": v(69.91, 1699.26) * mm, "construction": true});
            skLineSegment(sketch, "E155.0.0", {"start": v(-305.09, 1716.76) * mm, "end": v(-155.09, 1716.76) * mm, "construction": true});
            skLineSegment(sketch, "E156.0.0", {"start": v(-155.09, 1680.76) * mm, "end": v(-305.09, 1680.76) * mm, "construction": true});
            skLineSegment(sketch, "E157", {"start": v(-190.09, 1711.76) * mm, "end": v(-190.09, 1685.76) * mm});
            skLineSegment(sketch, "E158", {"start": v(-155.09, 1711.76) * mm, "end": v(-155.09, 1716.76) * mm});
            skLineSegment(sketch, "E159", {"start": v(-155.09, 1716.76) * mm, "end": v(69.91, 1716.76) * mm});
            skLineSegment(sketch, "E160", {"start": v(69.91, 1716.76) * mm, "end": v(69.91, 1680.76) * mm, "construction": true});
            skLineSegment(sketch, "E161", {"start": v(69.91, 1680.76) * mm, "end": v(-155.09, 1680.76) * mm});
            skLineSegment(sketch, "E162.bottom", {"start": v(-180.09, 1716.76) * mm, "end": v(-165.09, 1716.76) * mm});
            skLineSegment(sketch, "E162.top", {"start": v(-180.09, 1680.76) * mm, "end": v(-165.09, 1680.76) * mm});
            skLineSegment(sketch, "E162.right", {"start": v(-165.09, 1716.76) * mm, "end": v(-165.09, 1711.76) * mm});
            skLineSegment(sketch, "E163", {"start": v(-180.09, 1711.76) * mm, "end": v(-180.09, 1685.76) * mm, "construction": true});
            skLineSegment(sketch, "E164", {"start": v(-165.09, 1711.76) * mm, "end": v(-165.09, 1685.76) * mm, "construction": true});
            skLineSegment(sketch, "E165", {"start": v(-165.09, 1711.76) * mm, "end": v(-155.09, 1711.76) * mm});
            skLineSegment(sketch, "E166", {"start": v(-180.09, 1685.76) * mm, "end": v(-180.09, 1680.76) * mm});
            skLineSegment(sketch, "E167", {"start": v(-165.09, 1685.76) * mm, "end": v(-165.09, 1680.76) * mm});
            skLineSegment(sketch, "E168", {"start": v(-190.09, 1685.76) * mm, "end": v(-180.09, 1685.76) * mm});
            skLineSegment(sketch, "E169", {"start": v(-165.09, 1685.76) * mm, "end": v(-165.09, 1685.76) * mm});
            skLineSegment(sketch, "E170", {"start": v(-155.09, 1685.76) * mm, "end": v(-155.09, 1680.76) * mm});
            skLineSegment(sketch, "E171", {"start": v(69.91, 1716.76) * mm, "end": v(85.01, 1716.76) * mm});
            skLineSegment(sketch, "E172", {"start": v(100.01, 1701.76) * mm, "end": v(100.01, 1695.76) * mm});
            skLineSegment(sketch, "E173", {"start": v(85.01, 1680.76) * mm, "end": v(69.91, 1680.76) * mm});
            skLineSegment(sketch, "E174.bottom", {"start": v(51.81, 1701.36) * mm, "end": v(88.01, 1701.36) * mm});
            skLineSegment(sketch, "E174.top", {"start": v(51.81, 1696.16) * mm, "end": v(88.01, 1696.16) * mm});
            skLineSegment(sketch, "E174.left", {"start": v(51.81, 1701.36) * mm, "end": v(51.81, 1696.16) * mm});
            skLineSegment(sketch, "E174.right", {"start": v(88.01, 1701.36) * mm, "end": v(88.01, 1696.16) * mm});
            skPoint(sketch, "E175", {"position": v(88.01, 1698.76) * mm});
            skPoint(sketch, "E176", {"position": v(69.91, 1698.76) * mm});
            skPoint(sketch, "E177", {"position": v(69.91, 1701.36) * mm});
            skLineSegment(sketch, "E178", {"start": v(-165.09, 1685.76) * mm, "end": v(-155.09, 1685.76) * mm});
            skLineSegment(sketch, "E179", {"start": v(-180.09, 1716.76) * mm, "end": v(-180.09, 1711.76) * mm});
            skLineSegment(sketch, "E180", {"start": v(-190.09, 1711.76) * mm, "end": v(-180.09, 1711.76) * mm});
            skPoint(sketch, "E181.visualSharp", {"position": v(100.01, 1716.76) * mm});
            skArc(sketch, "E181.filletArc", {"start": v(100.01, 1701.76) * mm, "mid": v(95.62, 1712.37) * mm, "end": v(85.01, 1716.76) * mm});
            skPoint(sketch, "E182.visualSharp", {"position": v(100.01, 1680.76) * mm});
            skArc(sketch, "E182.filletArc", {"start": v(85.01, 1680.76) * mm, "mid": v(95.62, 1685.16) * mm, "end": v(100.01, 1695.76) * mm});
            skLineSegment(sketch, "E183", {"start": v(-144.09, 1711.76) * mm, "end": v(-144.09, 1685.76) * mm});
            skLineSegment(sketch, "E184", {"start": v(-144.09, 1685.76) * mm, "end": v(-118.09, 1685.76) * mm});
            skLineSegment(sketch, "E185", {"start": v(-118.09, 1685.76) * mm, "end": v(-144.09, 1711.76) * mm});
            skLineSegment(sketch, "E186", {"start": v(-133.1, 1711.76) * mm, "end": v(-107.1, 1685.76) * mm});
            skLineSegment(sketch, "E187", {"start": v(-107.1, 1685.76) * mm, "end": v(-81.1, 1711.76) * mm});
            skLineSegment(sketch, "E188", {"start": v(-81.1, 1711.76) * mm, "end": v(-133.1, 1711.76) * mm});
            skLineSegment(sketch, "E189", {"start": v(-70.13, 1711.76) * mm, "end": v(-96.13, 1685.76) * mm});
            skLineSegment(sketch, "E190", {"start": v(-96.13, 1685.76) * mm, "end": v(-44.13, 1685.76) * mm});
            skLineSegment(sketch, "E191", {"start": v(-44.13, 1685.76) * mm, "end": v(-70.13, 1711.76) * mm});
            skLineSegment(sketch, "E192", {"start": v(-59.15, 1711.76) * mm, "end": v(-33.15, 1685.76) * mm});
            skLineSegment(sketch, "E193", {"start": v(-33.15, 1685.76) * mm, "end": v(-7.15, 1711.76) * mm});
            skLineSegment(sketch, "E194", {"start": v(-7.15, 1711.76) * mm, "end": v(-59.15, 1711.76) * mm});
            skLineSegment(sketch, "E195", {"start": v(3.83, 1711.76) * mm, "end": v(-22.17, 1685.76) * mm});
            skLineSegment(sketch, "E196", {"start": v(-22.17, 1685.76) * mm, "end": v(29.83, 1685.76) * mm});
            skLineSegment(sketch, "E197", {"start": v(29.83, 1685.76) * mm, "end": v(3.83, 1711.76) * mm});
            skLineSegment(sketch, "E198", {"start": v(14.81, 1711.76) * mm, "end": v(40.81, 1685.76) * mm});
            skLineSegment(sketch, "E199", {"start": v(40.81, 1685.76) * mm, "end": v(40.81, 1711.76) * mm});
            skLineSegment(sketch, "E200", {"start": v(40.81, 1711.76) * mm, "end": v(14.81, 1711.76) * mm});
            skLineSegment(sketch, "E201", {"start": v(-144.09, 1711.76) * mm, "end": v(-133.1, 1711.76) * mm, "construction": true});
            skLineSegment(sketch, "E202", {"start": v(-81.1, 1711.76) * mm, "end": v(-70.13, 1711.76) * mm, "construction": true});
            skLineSegment(sketch, "E203", {"start": v(-70.13, 1711.76) * mm, "end": v(-59.15, 1711.76) * mm, "construction": true});
            skLineSegment(sketch, "E204", {"start": v(-7.15, 1711.76) * mm, "end": v(3.83, 1711.76) * mm, "construction": true});
            skLineSegment(sketch, "E205", {"start": v(3.83, 1711.76) * mm, "end": v(14.81, 1711.76) * mm, "construction": true});
            skLineSegment(sketch, "E206", {"start": v(85.01, 1701.76) * mm, "end": v(85.01, 1695.76) * mm, "construction": true});
            skLineSegment(sketch, "E207", {"start": v(85.01, 1698.76) * mm, "end": v(100.01, 1698.76) * mm, "construction": true});
            skSolve(sketch);
        }
        {
            var Q0;
            Q0 = qSketchRegion(id + "F48", true);
            extrude(context, id + "F49", {"entities" : qUnion([Q0]), "endBound" : BoundingType.SYMMETRIC, "depth" : 5 * mm});
        }
        {
            var Q0;
            Q0=makeQuery(id+"F49.opExtrude","SWEPT_EDGE",EDGE,{"disambiguationData":[OSD([sQuery(id+"F48.wireOp",EDGE,"E192"),sQuery(id+"F48.wireOp",EDGE,"E193")])]});
            chamfer(context, id + "F50", {"entities" : qUnion([Q0]), "width" : 10 * mm, "tangentPropagation" : true});
        }
        {
            var Q0;
            Q0=makeQuery(id+"F49.opExtrude","SWEPT_EDGE",EDGE,{"disambiguationData":[OSD([sQuery(id+"F48.wireOp",EDGE,"E189"),sQuery(id+"F48.wireOp",EDGE,"E191")])]});
            var Q1;
            Q1=makeQuery(id+"F49.opExtrude","SWEPT_EDGE",EDGE,{"disambiguationData":[OSD([sQuery(id+"F48.wireOp",EDGE,"E195"),sQuery(id+"F48.wireOp",EDGE,"E197")])]});
            var Q2;
            Q2=makeQuery(id+"F49.opExtrude","SWEPT_EDGE",EDGE,{"disambiguationData":[OSD([sQuery(id+"F48.wireOp",EDGE,"E186"),sQuery(id+"F48.wireOp",EDGE,"E187")])]});
            var Q3;
            Q3=makeQuery(id+"F49.opExtrude","SWEPT_EDGE",EDGE,{"disambiguationData":[OSD([sQuery(id+"F48.wireOp",EDGE,"E183"),sQuery(id+"F48.wireOp",EDGE,"E184")])]});
            var Q4;
            Q4=makeQuery(id+"F49.opExtrude","SWEPT_EDGE",EDGE,{"disambiguationData":[OSD([sQuery(id+"F48.wireOp",EDGE,"E186"),sQuery(id+"F48.wireOp",EDGE,"E188")])]});
            var Q5;
            Q5=makeQuery(id+"F49.opExtrude","SWEPT_EDGE",EDGE,{"disambiguationData":[OSD([sQuery(id+"F48.wireOp",EDGE,"E187"),sQuery(id+"F48.wireOp",EDGE,"E188")])]});
            var Q6;
            Q6=makeQuery(id+"F49.opExtrude","SWEPT_EDGE",EDGE,{"disambiguationData":[OSD([sQuery(id+"F48.wireOp",EDGE,"E192"),sQuery(id+"F48.wireOp",EDGE,"E194")])]});
            var Q7;
            Q7=makeQuery(id+"F49.opExtrude","SWEPT_EDGE",EDGE,{"disambiguationData":[OSD([sQuery(id+"F48.wireOp",EDGE,"E193"),sQuery(id+"F48.wireOp",EDGE,"E194")])]});
            var Q8;
            Q8=makeQuery(id+"F49.opExtrude","SWEPT_EDGE",EDGE,{"disambiguationData":[OSD([sQuery(id+"F48.wireOp",EDGE,"E190"),sQuery(id+"F48.wireOp",EDGE,"E191")])]});
            var Q9;
            Q9=makeQuery(id+"F49.opExtrude","SWEPT_EDGE",EDGE,{"disambiguationData":[OSD([sQuery(id+"F48.wireOp",EDGE,"E189"),sQuery(id+"F48.wireOp",EDGE,"E190")])]});
            var Q10;
            Q10=makeQuery(id+"F49.opExtrude","SWEPT_EDGE",EDGE,{"disambiguationData":[OSD([sQuery(id+"F48.wireOp",EDGE,"E195"),sQuery(id+"F48.wireOp",EDGE,"E196")])]});
            var Q11;
            Q11=makeQuery(id+"F49.opExtrude","SWEPT_EDGE",EDGE,{"disambiguationData":[OSD([sQuery(id+"F48.wireOp",EDGE,"E196"),sQuery(id+"F48.wireOp",EDGE,"E197")])]});
            var Q12;
            Q12=makeQuery(id+"F49.opExtrude","SWEPT_EDGE",EDGE,{"disambiguationData":[OSD([sQuery(id+"F48.wireOp",EDGE,"E199"),sQuery(id+"F48.wireOp",EDGE,"E200")])]});
            var Q13;
            {var subQ0=sQuery(id+"F48.wireOp",EDGE,"E192");Q13=makeQuery(id+"F50.opChamfer","BLEND_EDGE",EDGE,{"blendedFrom":[makeQuery(id+"F49.opExtrude","SWEPT_EDGE",EDGE,{"disambiguationData":[OSD([subQ0,sQuery(id+"F48.wireOp",EDGE,"E193")])]}),makeQuery(id+"F49.opExtrude","SWEPT_FACE",FACE,{"disambiguationData":[OSD([subQ0])]})],"blendedInto":[makeQuery(id+"F49.opExtrude","SWEPT_FACE",FACE,{"disambiguationData":[OSD([subQ0])]})]});}
            var Q14;
            {var subQ0=sQuery(id+"F48.wireOp",EDGE,"E193");Q14=makeQuery(id+"F50.opChamfer","BLEND_EDGE",EDGE,{"blendedFrom":[makeQuery(id+"F49.opExtrude","SWEPT_EDGE",EDGE,{"disambiguationData":[OSD([sQuery(id+"F48.wireOp",EDGE,"E192"),subQ0])]}),makeQuery(id+"F49.opExtrude","SWEPT_FACE",FACE,{"disambiguationData":[OSD([subQ0])]})],"blendedInto":[makeQuery(id+"F49.opExtrude","SWEPT_FACE",FACE,{"disambiguationData":[OSD([subQ0])]})]});}
            fillet(context, id + "F51", {"entities" : qUnion([Q0, Q1, Q2, Q3, Q4, Q5, Q6, Q7, Q8, Q9, Q10, Q11, Q12, Q13, Q14]), "radius" : 5 * mm, "tangentPropagation" : true, "allowEdgeOverflow" : false});
        }
        {
            var Q0;
            Q0=makeQuery(id+"F49.opExtrude","SWEPT_EDGE",EDGE,{"disambiguationData":[OSD([sQuery(id+"F48.wireOp",EDGE,"E183"),sQuery(id+"F48.wireOp",EDGE,"E185")])]});
            var Q1;
            Q1=makeQuery(id+"F49.opExtrude","SWEPT_EDGE",EDGE,{"disambiguationData":[OSD([sQuery(id+"F48.wireOp",EDGE,"E184"),sQuery(id+"F48.wireOp",EDGE,"E185")])]});
            var Q2;
            Q2=makeQuery(id+"F49.opExtrude","SWEPT_EDGE",EDGE,{"disambiguationData":[OSD([sQuery(id+"F48.wireOp",EDGE,"E198"),sQuery(id+"F48.wireOp",EDGE,"E200")])]});
            var Q3;
            Q3=makeQuery(id+"F49.opExtrude","SWEPT_EDGE",EDGE,{"disambiguationData":[OSD([sQuery(id+"F48.wireOp",EDGE,"E198"),sQuery(id+"F48.wireOp",EDGE,"E199")])]});
            fillet(context, id + "F52", {"entities" : qUnion([Q0, Q1, Q2, Q3]), "radius" : 2.5 * mm, "tangentPropagation" : true, "allowEdgeOverflow" : false});
        }
        {
            var Q0;
            Q0=makeQuery(id+"F49.opExtrude","CAP_FACE",FACE,{"disambiguationData":[OSD([sQuery(id+"F48.wireOp",EDGE,"E157"),sQuery(id+"F48.wireOp",EDGE,"E158"),sQuery(id+"F48.wireOp",EDGE,"E159"),sQuery(id+"F48.wireOp",EDGE,"E161"),sQuery(id+"F48.wireOp",EDGE,"E162.bottom"),sQuery(id+"F48.wireOp",EDGE,"E162.top"),sQuery(id+"F48.wireOp",EDGE,"E162.right"),sQuery(id+"F48.wireOp",EDGE,"E166"),sQuery(id+"F48.wireOp",EDGE,"E167"),sQuery(id+"F48.wireOp",EDGE,"E168"),sQuery(id+"F48.wireOp",EDGE,"E165"),sQuery(id+"F48.wireOp",EDGE,"E170"),sQuery(id+"F48.wireOp",EDGE,"E171"),sQuery(id+"F48.wireOp",EDGE,"E172"),sQuery(id+"F48.wireOp",EDGE,"E173"),sQuery(id+"F48.wireOp",EDGE,"E174.bottom"),sQuery(id+"F48.wireOp",EDGE,"E174.top"),sQuery(id+"F48.wireOp",EDGE,"E174.left"),sQuery(id+"F48.wireOp",EDGE,"E174.right"),sQuery(id+"F48.wireOp",EDGE,"E178"),sQuery(id+"F48.wireOp",EDGE,"E179"),sQuery(id+"F48.wireOp",EDGE,"E180"),sQuery(id+"F48.wireOp",EDGE,"E181.filletArc"),sQuery(id+"F48.wireOp",EDGE,"E182.filletArc"),sQuery(id+"F48.wireOp",EDGE,"E183"),sQuery(id+"F48.wireOp",EDGE,"E184"),sQuery(id+"F48.wireOp",EDGE,"E185"),sQuery(id+"F48.wireOp",EDGE,"E186"),sQuery(id+"F48.wireOp",EDGE,"E187"),sQuery(id+"F48.wireOp",EDGE,"E188"),sQuery(id+"F48.wireOp",EDGE,"E189"),sQuery(id+"F48.wireOp",EDGE,"E190"),sQuery(id+"F48.wireOp",EDGE,"E191"),sQuery(id+"F48.wireOp",EDGE,"E192"),sQuery(id+"F48.wireOp",EDGE,"E193"),sQuery(id+"F48.wireOp",EDGE,"E194"),sQuery(id+"F48.wireOp",EDGE,"E195"),sQuery(id+"F48.wireOp",EDGE,"E196"),sQuery(id+"F48.wireOp",EDGE,"E197"),sQuery(id+"F48.wireOp",EDGE,"E198"),sQuery(id+"F48.wireOp",EDGE,"E199"),sQuery(id+"F48.wireOp",EDGE,"E200")])],"isStart":false});
            var sketch = newSketch(context, id + "F53", { "sketchPlane" : qUnion([Q0])});
            skLineSegment(sketch, "E208", {"start": v(-37.65, 1686.84) * mm, "end": v(-34.65, 1686.84) * mm, "construction": true});
            skLineSegment(sketch, "E209", {"start": v(-34.65, 1686.84) * mm, "end": v(-31.65, 1686.84) * mm, "construction": true});
            skLineSegment(sketch, "E210", {"start": v(-31.65, 1686.84) * mm, "end": v(-28.65, 1686.84) * mm, "construction": true});
            skCircle(sketch, "E211", {"center": v(-37.65, 1686.84) * mm, "radius": 1 * mm});
            skCircle(sketch, "E212", {"center": v(-34.65, 1686.84) * mm, "radius": 1 * mm});
            skCircle(sketch, "E213", {"center": v(-31.65, 1686.84) * mm, "radius": 1 * mm});
            skCircle(sketch, "E214", {"center": v(-28.65, 1686.84) * mm, "radius": 1 * mm});
            skLineSegment(sketch, "E215.0", {"start": v(-28.15, 1692.84) * mm, "end": v(-38.15, 1692.84) * mm, "construction": true});
            skLineSegment(sketch, "E216", {"start": v(-33.15, 1692.84) * mm, "end": v(-33.15, 1686.84) * mm, "construction": true});
            skLineSegment(sketch, "E217", {"start": v(-175.09, 1692.76) * mm, "end": v(-175.09, 1696.76) * mm, "construction": true});
            skLineSegment(sketch, "E218", {"start": v(-175.09, 1700.76) * mm, "end": v(-175.09, 1704.76) * mm, "construction": true});
            skLineSegment(sketch, "E219", {"start": v(-175.09, 1696.76) * mm, "end": v(-175.09, 1700.76) * mm, "construction": true});
            skCircle(sketch, "E220", {"center": v(-175.09, 1696.76) * mm, "radius": 1.5 * mm});
            skCircle(sketch, "E221", {"center": v(-175.09, 1692.76) * mm, "radius": 1.5 * mm});
            skCircle(sketch, "E222", {"center": v(-175.09, 1704.76) * mm, "radius": 1.5 * mm});
            skCircle(sketch, "E223", {"center": v(-175.09, 1700.76) * mm, "radius": 1.5 * mm});
            skPoint(sketch, "E224", {"position": v(-175.09, 1698.76) * mm});
            skLineSegment(sketch, "E225", {"start": v(-190.09, 1698.76) * mm, "end": v(-175.09, 1698.76) * mm, "construction": true});
            skCircle(sketch, "E226", {"center": v(74.41, 1701.36) * mm, "radius": 1 * mm});
            skCircle(sketch, "E227", {"center": v(71.41, 1701.36) * mm, "radius": 1 * mm});
            skCircle(sketch, "E228", {"center": v(68.41, 1701.36) * mm, "radius": 0.86 * mm});
            skLineSegment(sketch, "E229", {"start": v(65.41, 1701.36) * mm, "end": v(68.41, 1701.36) * mm, "construction": true});
            skLineSegment(sketch, "E230", {"start": v(68.41, 1701.36) * mm, "end": v(71.41, 1701.36) * mm, "construction": true});
            skLineSegment(sketch, "E231", {"start": v(71.41, 1701.36) * mm, "end": v(74.41, 1701.36) * mm, "construction": true});
            skCircle(sketch, "E232", {"center": v(65.41, 1701.36) * mm, "radius": 0.86 * mm});
            skPoint(sketch, "E233", {"position": v(69.91, 1701.36) * mm});
            skLineSegment(sketch, "E234.0", {"start": v(51.81, 1701.36) * mm, "end": v(88.01, 1701.36) * mm, "construction": true});
            skCircle(sketch, "E235", {"center": v(59.91, 1688.76) * mm, "radius": 1.25 * mm});
            skSolve(sketch);
        }
        {
            var Q0;
            Q0 = qSketchRegion(id + "F53", true);
            extrude(context, id + "F54", {"entities" : qUnion([Q0]), "operationType" : NewBodyOperationType.REMOVE, "oppositeDirection" : true, "depth" : 25 * mm});
        }
        {
            var Q0;
            Q0=makeQuery(id+"F49.opExtrude","SWEPT_BODY",BODY,{"disambiguationData":[OSD([sQuery(id+"F48.wireOp",EDGE,"E157"),sQuery(id+"F48.wireOp",EDGE,"E158"),sQuery(id+"F48.wireOp",EDGE,"E159"),sQuery(id+"F48.wireOp",EDGE,"E161"),sQuery(id+"F48.wireOp",EDGE,"E162.bottom"),sQuery(id+"F48.wireOp",EDGE,"E162.top"),sQuery(id+"F48.wireOp",EDGE,"E162.left"),sQuery(id+"F48.wireOp",EDGE,"E162.right"),sQuery(id+"F48.wireOp",EDGE,"E166"),sQuery(id+"F48.wireOp",EDGE,"E167"),sQuery(id+"F48.wireOp",EDGE,"79368569-35d3-4e95-8ebc-8ec5569dfd2e"),sQuery(id+"F48.wireOp",EDGE,"E168"),sQuery(id+"F48.wireOp",EDGE,"E165"),sQuery(id+"F48.wireOp",EDGE,"E170"),sQuery(id+"F48.wireOp",EDGE,"E171"),sQuery(id+"F48.wireOp",EDGE,"E172"),sQuery(id+"F48.wireOp",EDGE,"E173"),sQuery(id+"F48.wireOp",EDGE,"E174.bottom"),sQuery(id+"F48.wireOp",EDGE,"E174.top"),sQuery(id+"F48.wireOp",EDGE,"E174.left"),sQuery(id+"F48.wireOp",EDGE,"E174.right"),sQuery(id+"F48.wireOp",EDGE,"E178")])]});
            var Q1;
            Q1=sQuery(id+"F0.wireOp",EDGE,"E6");
            circularPattern(context, id + "F55", {"entities" : qUnion([Q0]), "axis" : qUnion([Q1]), "angle" : 360 * degree, "instanceCount" : 12, "equalSpace" : true});
        }
        {
            var Q0;
            Q0=makeQuery(id+"F55.opPattern","COPY",BODY,{"derivedFrom":makeQuery(id+"F49.opExtrude","SWEPT_BODY",BODY,{"disambiguationData":[OSD([sQuery(id+"F48.wireOp",EDGE,"E157"),sQuery(id+"F48.wireOp",EDGE,"E158"),sQuery(id+"F48.wireOp",EDGE,"E159"),sQuery(id+"F48.wireOp",EDGE,"E161"),sQuery(id+"F48.wireOp",EDGE,"E162.bottom"),sQuery(id+"F48.wireOp",EDGE,"E162.top"),sQuery(id+"F48.wireOp",EDGE,"E162.right"),sQuery(id+"F48.wireOp",EDGE,"E166"),sQuery(id+"F48.wireOp",EDGE,"E167"),sQuery(id+"F48.wireOp",EDGE,"E168"),sQuery(id+"F48.wireOp",EDGE,"E165"),sQuery(id+"F48.wireOp",EDGE,"E170"),sQuery(id+"F48.wireOp",EDGE,"E171"),sQuery(id+"F48.wireOp",EDGE,"E172"),sQuery(id+"F48.wireOp",EDGE,"E173"),sQuery(id+"F48.wireOp",EDGE,"E174.bottom"),sQuery(id+"F48.wireOp",EDGE,"E174.top"),sQuery(id+"F48.wireOp",EDGE,"E174.left"),sQuery(id+"F48.wireOp",EDGE,"E174.right"),sQuery(id+"F48.wireOp",EDGE,"E178"),sQuery(id+"F48.wireOp",EDGE,"E179"),sQuery(id+"F48.wireOp",EDGE,"E180")])]}),"instanceName":"17"});
            var Q1;
            Q1=makeQuery(id+"F49.opExtrude","SWEPT_BODY",BODY,{"disambiguationData":[OSD([sQuery(id+"F48.wireOp",EDGE,"E157"),sQuery(id+"F48.wireOp",EDGE,"E158"),sQuery(id+"F48.wireOp",EDGE,"E159"),sQuery(id+"F48.wireOp",EDGE,"E161"),sQuery(id+"F48.wireOp",EDGE,"E162.bottom"),sQuery(id+"F48.wireOp",EDGE,"E162.top"),sQuery(id+"F48.wireOp",EDGE,"E162.right"),sQuery(id+"F48.wireOp",EDGE,"E166"),sQuery(id+"F48.wireOp",EDGE,"E167"),sQuery(id+"F48.wireOp",EDGE,"E168"),sQuery(id+"F48.wireOp",EDGE,"E165"),sQuery(id+"F48.wireOp",EDGE,"E170"),sQuery(id+"F48.wireOp",EDGE,"E171"),sQuery(id+"F48.wireOp",EDGE,"E172"),sQuery(id+"F48.wireOp",EDGE,"E173"),sQuery(id+"F48.wireOp",EDGE,"E174.bottom"),sQuery(id+"F48.wireOp",EDGE,"E174.top"),sQuery(id+"F48.wireOp",EDGE,"E174.left"),sQuery(id+"F48.wireOp",EDGE,"E174.right"),sQuery(id+"F48.wireOp",EDGE,"E178"),sQuery(id+"F48.wireOp",EDGE,"E179"),sQuery(id+"F48.wireOp",EDGE,"E180")])]});
            var Q2;
            Q2=makeQuery(id+"F55.opPattern","COPY",BODY,{"derivedFrom":makeQuery(id+"F49.opExtrude","SWEPT_BODY",BODY,{"disambiguationData":[OSD([sQuery(id+"F48.wireOp",EDGE,"E157"),sQuery(id+"F48.wireOp",EDGE,"E158"),sQuery(id+"F48.wireOp",EDGE,"E159"),sQuery(id+"F48.wireOp",EDGE,"E161"),sQuery(id+"F48.wireOp",EDGE,"E162.bottom"),sQuery(id+"F48.wireOp",EDGE,"E162.top"),sQuery(id+"F48.wireOp",EDGE,"E162.right"),sQuery(id+"F48.wireOp",EDGE,"E166"),sQuery(id+"F48.wireOp",EDGE,"E167"),sQuery(id+"F48.wireOp",EDGE,"E168"),sQuery(id+"F48.wireOp",EDGE,"E165"),sQuery(id+"F48.wireOp",EDGE,"E170"),sQuery(id+"F48.wireOp",EDGE,"E171"),sQuery(id+"F48.wireOp",EDGE,"E172"),sQuery(id+"F48.wireOp",EDGE,"E173"),sQuery(id+"F48.wireOp",EDGE,"E174.bottom"),sQuery(id+"F48.wireOp",EDGE,"E174.top"),sQuery(id+"F48.wireOp",EDGE,"E174.left"),sQuery(id+"F48.wireOp",EDGE,"E174.right"),sQuery(id+"F48.wireOp",EDGE,"E178"),sQuery(id+"F48.wireOp",EDGE,"E179"),sQuery(id+"F48.wireOp",EDGE,"E180")])]}),"instanceName":"1"});
            var Q3;
            Q3=makeQuery(id+"F55.opPattern","COPY",BODY,{"derivedFrom":makeQuery(id+"F49.opExtrude","SWEPT_BODY",BODY,{"disambiguationData":[OSD([sQuery(id+"F48.wireOp",EDGE,"E157"),sQuery(id+"F48.wireOp",EDGE,"E158"),sQuery(id+"F48.wireOp",EDGE,"E159"),sQuery(id+"F48.wireOp",EDGE,"E161"),sQuery(id+"F48.wireOp",EDGE,"E162.bottom"),sQuery(id+"F48.wireOp",EDGE,"E162.top"),sQuery(id+"F48.wireOp",EDGE,"E162.right"),sQuery(id+"F48.wireOp",EDGE,"E166"),sQuery(id+"F48.wireOp",EDGE,"E167"),sQuery(id+"F48.wireOp",EDGE,"E168"),sQuery(id+"F48.wireOp",EDGE,"E165"),sQuery(id+"F48.wireOp",EDGE,"E170"),sQuery(id+"F48.wireOp",EDGE,"E171"),sQuery(id+"F48.wireOp",EDGE,"E172"),sQuery(id+"F48.wireOp",EDGE,"E173"),sQuery(id+"F48.wireOp",EDGE,"E174.bottom"),sQuery(id+"F48.wireOp",EDGE,"E174.top"),sQuery(id+"F48.wireOp",EDGE,"E174.left"),sQuery(id+"F48.wireOp",EDGE,"E174.right"),sQuery(id+"F48.wireOp",EDGE,"E178"),sQuery(id+"F48.wireOp",EDGE,"E179"),sQuery(id+"F48.wireOp",EDGE,"E180")])]}),"instanceName":"2"});
            var Q4;
            Q4=makeQuery(id+"F55.opPattern","COPY",BODY,{"derivedFrom":makeQuery(id+"F49.opExtrude","SWEPT_BODY",BODY,{"disambiguationData":[OSD([sQuery(id+"F48.wireOp",EDGE,"E157"),sQuery(id+"F48.wireOp",EDGE,"E158"),sQuery(id+"F48.wireOp",EDGE,"E159"),sQuery(id+"F48.wireOp",EDGE,"E161"),sQuery(id+"F48.wireOp",EDGE,"E162.bottom"),sQuery(id+"F48.wireOp",EDGE,"E162.top"),sQuery(id+"F48.wireOp",EDGE,"E162.right"),sQuery(id+"F48.wireOp",EDGE,"E166"),sQuery(id+"F48.wireOp",EDGE,"E167"),sQuery(id+"F48.wireOp",EDGE,"E168"),sQuery(id+"F48.wireOp",EDGE,"E165"),sQuery(id+"F48.wireOp",EDGE,"E170"),sQuery(id+"F48.wireOp",EDGE,"E171"),sQuery(id+"F48.wireOp",EDGE,"E172"),sQuery(id+"F48.wireOp",EDGE,"E173"),sQuery(id+"F48.wireOp",EDGE,"E174.bottom"),sQuery(id+"F48.wireOp",EDGE,"E174.top"),sQuery(id+"F48.wireOp",EDGE,"E174.left"),sQuery(id+"F48.wireOp",EDGE,"E174.right"),sQuery(id+"F48.wireOp",EDGE,"E178"),sQuery(id+"F48.wireOp",EDGE,"E179"),sQuery(id+"F48.wireOp",EDGE,"E180")])]}),"instanceName":"3"});
            var Q5;
            Q5=makeQuery(id+"F55.opPattern","COPY",BODY,{"derivedFrom":makeQuery(id+"F49.opExtrude","SWEPT_BODY",BODY,{"disambiguationData":[OSD([sQuery(id+"F48.wireOp",EDGE,"E157"),sQuery(id+"F48.wireOp",EDGE,"E158"),sQuery(id+"F48.wireOp",EDGE,"E159"),sQuery(id+"F48.wireOp",EDGE,"E161"),sQuery(id+"F48.wireOp",EDGE,"E162.bottom"),sQuery(id+"F48.wireOp",EDGE,"E162.top"),sQuery(id+"F48.wireOp",EDGE,"E162.right"),sQuery(id+"F48.wireOp",EDGE,"E166"),sQuery(id+"F48.wireOp",EDGE,"E167"),sQuery(id+"F48.wireOp",EDGE,"E168"),sQuery(id+"F48.wireOp",EDGE,"E165"),sQuery(id+"F48.wireOp",EDGE,"E170"),sQuery(id+"F48.wireOp",EDGE,"E171"),sQuery(id+"F48.wireOp",EDGE,"E172"),sQuery(id+"F48.wireOp",EDGE,"E173"),sQuery(id+"F48.wireOp",EDGE,"E174.bottom"),sQuery(id+"F48.wireOp",EDGE,"E174.top"),sQuery(id+"F48.wireOp",EDGE,"E174.left"),sQuery(id+"F48.wireOp",EDGE,"E174.right"),sQuery(id+"F48.wireOp",EDGE,"E178"),sQuery(id+"F48.wireOp",EDGE,"E179"),sQuery(id+"F48.wireOp",EDGE,"E180")])]}),"instanceName":"4"});
            var Q6;
            Q6=makeQuery(id+"F55.opPattern","COPY",BODY,{"derivedFrom":makeQuery(id+"F49.opExtrude","SWEPT_BODY",BODY,{"disambiguationData":[OSD([sQuery(id+"F48.wireOp",EDGE,"E157"),sQuery(id+"F48.wireOp",EDGE,"E158"),sQuery(id+"F48.wireOp",EDGE,"E159"),sQuery(id+"F48.wireOp",EDGE,"E161"),sQuery(id+"F48.wireOp",EDGE,"E162.bottom"),sQuery(id+"F48.wireOp",EDGE,"E162.top"),sQuery(id+"F48.wireOp",EDGE,"E162.right"),sQuery(id+"F48.wireOp",EDGE,"E166"),sQuery(id+"F48.wireOp",EDGE,"E167"),sQuery(id+"F48.wireOp",EDGE,"E168"),sQuery(id+"F48.wireOp",EDGE,"E165"),sQuery(id+"F48.wireOp",EDGE,"E170"),sQuery(id+"F48.wireOp",EDGE,"E171"),sQuery(id+"F48.wireOp",EDGE,"E172"),sQuery(id+"F48.wireOp",EDGE,"E173"),sQuery(id+"F48.wireOp",EDGE,"E174.bottom"),sQuery(id+"F48.wireOp",EDGE,"E174.top"),sQuery(id+"F48.wireOp",EDGE,"E174.left"),sQuery(id+"F48.wireOp",EDGE,"E174.right"),sQuery(id+"F48.wireOp",EDGE,"E178"),sQuery(id+"F48.wireOp",EDGE,"E179"),sQuery(id+"F48.wireOp",EDGE,"E180")])]}),"instanceName":"5"});
            var Q7;
            Q7=makeQuery(id+"F55.opPattern","COPY",BODY,{"derivedFrom":makeQuery(id+"F49.opExtrude","SWEPT_BODY",BODY,{"disambiguationData":[OSD([sQuery(id+"F48.wireOp",EDGE,"E157"),sQuery(id+"F48.wireOp",EDGE,"E158"),sQuery(id+"F48.wireOp",EDGE,"E159"),sQuery(id+"F48.wireOp",EDGE,"E161"),sQuery(id+"F48.wireOp",EDGE,"E162.bottom"),sQuery(id+"F48.wireOp",EDGE,"E162.top"),sQuery(id+"F48.wireOp",EDGE,"E162.right"),sQuery(id+"F48.wireOp",EDGE,"E166"),sQuery(id+"F48.wireOp",EDGE,"E167"),sQuery(id+"F48.wireOp",EDGE,"E168"),sQuery(id+"F48.wireOp",EDGE,"E165"),sQuery(id+"F48.wireOp",EDGE,"E170"),sQuery(id+"F48.wireOp",EDGE,"E171"),sQuery(id+"F48.wireOp",EDGE,"E172"),sQuery(id+"F48.wireOp",EDGE,"E173"),sQuery(id+"F48.wireOp",EDGE,"E174.bottom"),sQuery(id+"F48.wireOp",EDGE,"E174.top"),sQuery(id+"F48.wireOp",EDGE,"E174.left"),sQuery(id+"F48.wireOp",EDGE,"E174.right"),sQuery(id+"F48.wireOp",EDGE,"E178"),sQuery(id+"F48.wireOp",EDGE,"E179"),sQuery(id+"F48.wireOp",EDGE,"E180")])]}),"instanceName":"6"});
            var Q8;
            Q8=makeQuery(id+"F55.opPattern","COPY",BODY,{"derivedFrom":makeQuery(id+"F49.opExtrude","SWEPT_BODY",BODY,{"disambiguationData":[OSD([sQuery(id+"F48.wireOp",EDGE,"E157"),sQuery(id+"F48.wireOp",EDGE,"E158"),sQuery(id+"F48.wireOp",EDGE,"E159"),sQuery(id+"F48.wireOp",EDGE,"E161"),sQuery(id+"F48.wireOp",EDGE,"E162.bottom"),sQuery(id+"F48.wireOp",EDGE,"E162.top"),sQuery(id+"F48.wireOp",EDGE,"E162.right"),sQuery(id+"F48.wireOp",EDGE,"E166"),sQuery(id+"F48.wireOp",EDGE,"E167"),sQuery(id+"F48.wireOp",EDGE,"E168"),sQuery(id+"F48.wireOp",EDGE,"E165"),sQuery(id+"F48.wireOp",EDGE,"E170"),sQuery(id+"F48.wireOp",EDGE,"E171"),sQuery(id+"F48.wireOp",EDGE,"E172"),sQuery(id+"F48.wireOp",EDGE,"E173"),sQuery(id+"F48.wireOp",EDGE,"E174.bottom"),sQuery(id+"F48.wireOp",EDGE,"E174.top"),sQuery(id+"F48.wireOp",EDGE,"E174.left"),sQuery(id+"F48.wireOp",EDGE,"E174.right"),sQuery(id+"F48.wireOp",EDGE,"E178"),sQuery(id+"F48.wireOp",EDGE,"E179"),sQuery(id+"F48.wireOp",EDGE,"E180")])]}),"instanceName":"7"});
            var Q9;
            Q9=makeQuery(id+"F55.opPattern","COPY",BODY,{"derivedFrom":makeQuery(id+"F49.opExtrude","SWEPT_BODY",BODY,{"disambiguationData":[OSD([sQuery(id+"F48.wireOp",EDGE,"E157"),sQuery(id+"F48.wireOp",EDGE,"E158"),sQuery(id+"F48.wireOp",EDGE,"E159"),sQuery(id+"F48.wireOp",EDGE,"E161"),sQuery(id+"F48.wireOp",EDGE,"E162.bottom"),sQuery(id+"F48.wireOp",EDGE,"E162.top"),sQuery(id+"F48.wireOp",EDGE,"E162.right"),sQuery(id+"F48.wireOp",EDGE,"E166"),sQuery(id+"F48.wireOp",EDGE,"E167"),sQuery(id+"F48.wireOp",EDGE,"E168"),sQuery(id+"F48.wireOp",EDGE,"E165"),sQuery(id+"F48.wireOp",EDGE,"E170"),sQuery(id+"F48.wireOp",EDGE,"E171"),sQuery(id+"F48.wireOp",EDGE,"E172"),sQuery(id+"F48.wireOp",EDGE,"E173"),sQuery(id+"F48.wireOp",EDGE,"E174.bottom"),sQuery(id+"F48.wireOp",EDGE,"E174.top"),sQuery(id+"F48.wireOp",EDGE,"E174.left"),sQuery(id+"F48.wireOp",EDGE,"E174.right"),sQuery(id+"F48.wireOp",EDGE,"E178"),sQuery(id+"F48.wireOp",EDGE,"E179"),sQuery(id+"F48.wireOp",EDGE,"E180")])]}),"instanceName":"8"});
            var Q10;
            Q10=makeQuery(id+"F55.opPattern","COPY",BODY,{"derivedFrom":makeQuery(id+"F49.opExtrude","SWEPT_BODY",BODY,{"disambiguationData":[OSD([sQuery(id+"F48.wireOp",EDGE,"E157"),sQuery(id+"F48.wireOp",EDGE,"E158"),sQuery(id+"F48.wireOp",EDGE,"E159"),sQuery(id+"F48.wireOp",EDGE,"E161"),sQuery(id+"F48.wireOp",EDGE,"E162.bottom"),sQuery(id+"F48.wireOp",EDGE,"E162.top"),sQuery(id+"F48.wireOp",EDGE,"E162.right"),sQuery(id+"F48.wireOp",EDGE,"E166"),sQuery(id+"F48.wireOp",EDGE,"E167"),sQuery(id+"F48.wireOp",EDGE,"E168"),sQuery(id+"F48.wireOp",EDGE,"E165"),sQuery(id+"F48.wireOp",EDGE,"E170"),sQuery(id+"F48.wireOp",EDGE,"E171"),sQuery(id+"F48.wireOp",EDGE,"E172"),sQuery(id+"F48.wireOp",EDGE,"E173"),sQuery(id+"F48.wireOp",EDGE,"E174.bottom"),sQuery(id+"F48.wireOp",EDGE,"E174.top"),sQuery(id+"F48.wireOp",EDGE,"E174.left"),sQuery(id+"F48.wireOp",EDGE,"E174.right"),sQuery(id+"F48.wireOp",EDGE,"E178"),sQuery(id+"F48.wireOp",EDGE,"E179"),sQuery(id+"F48.wireOp",EDGE,"E180")])]}),"instanceName":"9"});
            var Q11;
            Q11=makeQuery(id+"F55.opPattern","COPY",BODY,{"derivedFrom":makeQuery(id+"F49.opExtrude","SWEPT_BODY",BODY,{"disambiguationData":[OSD([sQuery(id+"F48.wireOp",EDGE,"E157"),sQuery(id+"F48.wireOp",EDGE,"E158"),sQuery(id+"F48.wireOp",EDGE,"E159"),sQuery(id+"F48.wireOp",EDGE,"E161"),sQuery(id+"F48.wireOp",EDGE,"E162.bottom"),sQuery(id+"F48.wireOp",EDGE,"E162.top"),sQuery(id+"F48.wireOp",EDGE,"E162.right"),sQuery(id+"F48.wireOp",EDGE,"E166"),sQuery(id+"F48.wireOp",EDGE,"E167"),sQuery(id+"F48.wireOp",EDGE,"E168"),sQuery(id+"F48.wireOp",EDGE,"E165"),sQuery(id+"F48.wireOp",EDGE,"E170"),sQuery(id+"F48.wireOp",EDGE,"E171"),sQuery(id+"F48.wireOp",EDGE,"E172"),sQuery(id+"F48.wireOp",EDGE,"E173"),sQuery(id+"F48.wireOp",EDGE,"E174.bottom"),sQuery(id+"F48.wireOp",EDGE,"E174.top"),sQuery(id+"F48.wireOp",EDGE,"E174.left"),sQuery(id+"F48.wireOp",EDGE,"E174.right"),sQuery(id+"F48.wireOp",EDGE,"E178"),sQuery(id+"F48.wireOp",EDGE,"E179"),sQuery(id+"F48.wireOp",EDGE,"E180")])]}),"instanceName":"10"});
            var Q12;
            Q12=makeQuery(id+"F55.opPattern","COPY",BODY,{"derivedFrom":makeQuery(id+"F49.opExtrude","SWEPT_BODY",BODY,{"disambiguationData":[OSD([sQuery(id+"F48.wireOp",EDGE,"E157"),sQuery(id+"F48.wireOp",EDGE,"E158"),sQuery(id+"F48.wireOp",EDGE,"E159"),sQuery(id+"F48.wireOp",EDGE,"E161"),sQuery(id+"F48.wireOp",EDGE,"E162.bottom"),sQuery(id+"F48.wireOp",EDGE,"E162.top"),sQuery(id+"F48.wireOp",EDGE,"E162.right"),sQuery(id+"F48.wireOp",EDGE,"E166"),sQuery(id+"F48.wireOp",EDGE,"E167"),sQuery(id+"F48.wireOp",EDGE,"E168"),sQuery(id+"F48.wireOp",EDGE,"E165"),sQuery(id+"F48.wireOp",EDGE,"E170"),sQuery(id+"F48.wireOp",EDGE,"E171"),sQuery(id+"F48.wireOp",EDGE,"E172"),sQuery(id+"F48.wireOp",EDGE,"E173"),sQuery(id+"F48.wireOp",EDGE,"E174.bottom"),sQuery(id+"F48.wireOp",EDGE,"E174.top"),sQuery(id+"F48.wireOp",EDGE,"E174.left"),sQuery(id+"F48.wireOp",EDGE,"E174.right"),sQuery(id+"F48.wireOp",EDGE,"E178"),sQuery(id+"F48.wireOp",EDGE,"E179"),sQuery(id+"F48.wireOp",EDGE,"E180")])]}),"instanceName":"11"});
            var Q13;
            Q13=makeQuery(id+"F55.opPattern","COPY",BODY,{"derivedFrom":makeQuery(id+"F49.opExtrude","SWEPT_BODY",BODY,{"disambiguationData":[OSD([sQuery(id+"F48.wireOp",EDGE,"E157"),sQuery(id+"F48.wireOp",EDGE,"E158"),sQuery(id+"F48.wireOp",EDGE,"E159"),sQuery(id+"F48.wireOp",EDGE,"E161"),sQuery(id+"F48.wireOp",EDGE,"E162.bottom"),sQuery(id+"F48.wireOp",EDGE,"E162.top"),sQuery(id+"F48.wireOp",EDGE,"E162.right"),sQuery(id+"F48.wireOp",EDGE,"E166"),sQuery(id+"F48.wireOp",EDGE,"E167"),sQuery(id+"F48.wireOp",EDGE,"E168"),sQuery(id+"F48.wireOp",EDGE,"E165"),sQuery(id+"F48.wireOp",EDGE,"E170"),sQuery(id+"F48.wireOp",EDGE,"E171"),sQuery(id+"F48.wireOp",EDGE,"E172"),sQuery(id+"F48.wireOp",EDGE,"E173"),sQuery(id+"F48.wireOp",EDGE,"E174.bottom"),sQuery(id+"F48.wireOp",EDGE,"E174.top"),sQuery(id+"F48.wireOp",EDGE,"E174.left"),sQuery(id+"F48.wireOp",EDGE,"E174.right"),sQuery(id+"F48.wireOp",EDGE,"E178"),sQuery(id+"F48.wireOp",EDGE,"E179"),sQuery(id+"F48.wireOp",EDGE,"E180")])]}),"instanceName":"12"});
            var Q14;
            Q14=makeQuery(id+"F55.opPattern","COPY",BODY,{"derivedFrom":makeQuery(id+"F49.opExtrude","SWEPT_BODY",BODY,{"disambiguationData":[OSD([sQuery(id+"F48.wireOp",EDGE,"E157"),sQuery(id+"F48.wireOp",EDGE,"E158"),sQuery(id+"F48.wireOp",EDGE,"E159"),sQuery(id+"F48.wireOp",EDGE,"E161"),sQuery(id+"F48.wireOp",EDGE,"E162.bottom"),sQuery(id+"F48.wireOp",EDGE,"E162.top"),sQuery(id+"F48.wireOp",EDGE,"E162.right"),sQuery(id+"F48.wireOp",EDGE,"E166"),sQuery(id+"F48.wireOp",EDGE,"E167"),sQuery(id+"F48.wireOp",EDGE,"E168"),sQuery(id+"F48.wireOp",EDGE,"E165"),sQuery(id+"F48.wireOp",EDGE,"E170"),sQuery(id+"F48.wireOp",EDGE,"E171"),sQuery(id+"F48.wireOp",EDGE,"E172"),sQuery(id+"F48.wireOp",EDGE,"E173"),sQuery(id+"F48.wireOp",EDGE,"E174.bottom"),sQuery(id+"F48.wireOp",EDGE,"E174.top"),sQuery(id+"F48.wireOp",EDGE,"E174.left"),sQuery(id+"F48.wireOp",EDGE,"E174.right"),sQuery(id+"F48.wireOp",EDGE,"E178"),sQuery(id+"F48.wireOp",EDGE,"E179"),sQuery(id+"F48.wireOp",EDGE,"E180")])]}),"instanceName":"13"});
            var Q15;
            Q15=makeQuery(id+"F55.opPattern","COPY",BODY,{"derivedFrom":makeQuery(id+"F49.opExtrude","SWEPT_BODY",BODY,{"disambiguationData":[OSD([sQuery(id+"F48.wireOp",EDGE,"E157"),sQuery(id+"F48.wireOp",EDGE,"E158"),sQuery(id+"F48.wireOp",EDGE,"E159"),sQuery(id+"F48.wireOp",EDGE,"E161"),sQuery(id+"F48.wireOp",EDGE,"E162.bottom"),sQuery(id+"F48.wireOp",EDGE,"E162.top"),sQuery(id+"F48.wireOp",EDGE,"E162.right"),sQuery(id+"F48.wireOp",EDGE,"E166"),sQuery(id+"F48.wireOp",EDGE,"E167"),sQuery(id+"F48.wireOp",EDGE,"E168"),sQuery(id+"F48.wireOp",EDGE,"E165"),sQuery(id+"F48.wireOp",EDGE,"E170"),sQuery(id+"F48.wireOp",EDGE,"E171"),sQuery(id+"F48.wireOp",EDGE,"E172"),sQuery(id+"F48.wireOp",EDGE,"E173"),sQuery(id+"F48.wireOp",EDGE,"E174.bottom"),sQuery(id+"F48.wireOp",EDGE,"E174.top"),sQuery(id+"F48.wireOp",EDGE,"E174.left"),sQuery(id+"F48.wireOp",EDGE,"E174.right"),sQuery(id+"F48.wireOp",EDGE,"E178"),sQuery(id+"F48.wireOp",EDGE,"E179"),sQuery(id+"F48.wireOp",EDGE,"E180")])]}),"instanceName":"14"});
            var Q16;
            Q16=makeQuery(id+"F55.opPattern","COPY",BODY,{"derivedFrom":makeQuery(id+"F49.opExtrude","SWEPT_BODY",BODY,{"disambiguationData":[OSD([sQuery(id+"F48.wireOp",EDGE,"E157"),sQuery(id+"F48.wireOp",EDGE,"E158"),sQuery(id+"F48.wireOp",EDGE,"E159"),sQuery(id+"F48.wireOp",EDGE,"E161"),sQuery(id+"F48.wireOp",EDGE,"E162.bottom"),sQuery(id+"F48.wireOp",EDGE,"E162.top"),sQuery(id+"F48.wireOp",EDGE,"E162.right"),sQuery(id+"F48.wireOp",EDGE,"E166"),sQuery(id+"F48.wireOp",EDGE,"E167"),sQuery(id+"F48.wireOp",EDGE,"E168"),sQuery(id+"F48.wireOp",EDGE,"E165"),sQuery(id+"F48.wireOp",EDGE,"E170"),sQuery(id+"F48.wireOp",EDGE,"E171"),sQuery(id+"F48.wireOp",EDGE,"E172"),sQuery(id+"F48.wireOp",EDGE,"E173"),sQuery(id+"F48.wireOp",EDGE,"E174.bottom"),sQuery(id+"F48.wireOp",EDGE,"E174.top"),sQuery(id+"F48.wireOp",EDGE,"E174.left"),sQuery(id+"F48.wireOp",EDGE,"E174.right"),sQuery(id+"F48.wireOp",EDGE,"E178"),sQuery(id+"F48.wireOp",EDGE,"E179"),sQuery(id+"F48.wireOp",EDGE,"E180")])]}),"instanceName":"15"});
            var Q17;
            Q17=makeQuery(id+"F55.opPattern","COPY",BODY,{"derivedFrom":makeQuery(id+"F49.opExtrude","SWEPT_BODY",BODY,{"disambiguationData":[OSD([sQuery(id+"F48.wireOp",EDGE,"E157"),sQuery(id+"F48.wireOp",EDGE,"E158"),sQuery(id+"F48.wireOp",EDGE,"E159"),sQuery(id+"F48.wireOp",EDGE,"E161"),sQuery(id+"F48.wireOp",EDGE,"E162.bottom"),sQuery(id+"F48.wireOp",EDGE,"E162.top"),sQuery(id+"F48.wireOp",EDGE,"E162.right"),sQuery(id+"F48.wireOp",EDGE,"E166"),sQuery(id+"F48.wireOp",EDGE,"E167"),sQuery(id+"F48.wireOp",EDGE,"E168"),sQuery(id+"F48.wireOp",EDGE,"E165"),sQuery(id+"F48.wireOp",EDGE,"E170"),sQuery(id+"F48.wireOp",EDGE,"E171"),sQuery(id+"F48.wireOp",EDGE,"E172"),sQuery(id+"F48.wireOp",EDGE,"E173"),sQuery(id+"F48.wireOp",EDGE,"E174.bottom"),sQuery(id+"F48.wireOp",EDGE,"E174.top"),sQuery(id+"F48.wireOp",EDGE,"E174.left"),sQuery(id+"F48.wireOp",EDGE,"E174.right"),sQuery(id+"F48.wireOp",EDGE,"E178"),sQuery(id+"F48.wireOp",EDGE,"E179"),sQuery(id+"F48.wireOp",EDGE,"E180")])]}),"instanceName":"16"});
            var Q18;
            Q18=makeQuery(id+"F46.opExtrude","SWEPT_BODY",BODY,{"disambiguationData":[OSD([sQuery(id+"F45.wireOp",EDGE,"E150"),sQuery(id+"F45.wireOp",EDGE,"E151")])]});
            var Q19;
            Q19=makeQuery(id+"F47.opPattern","COPY",BODY,{"derivedFrom":makeQuery(id+"F46.opExtrude","SWEPT_BODY",BODY,{"disambiguationData":[OSD([sQuery(id+"F45.wireOp",EDGE,"E150"),sQuery(id+"F45.wireOp",EDGE,"E151")])]}),"instanceName":"1"});
            booleanBodies(context, id + "F56", {"operationType" : BooleanOperationType.SUBTRACTION, "tools" : qUnion([Q0, Q1, Q2, Q3, Q4, Q5, Q6, Q7, Q8, Q9, Q10, Q11, Q12, Q13, Q14, Q15, Q16, Q17]), "targets" : qUnion([Q18, Q19]), "keepTools" : true});
        }
        {
            var Q0;
            Q0=qCreatedBy(id+"F44.planeOp",FACE);
            var sketch = newSketch(context, id + "F57", { "sketchPlane" : qUnion([Q0])});
            skCircle(sketch, "E236.0", {"center": v(0, -230.09) * mm, "radius": 75 * mm, "construction": true});
            skLineSegment(sketch, "E237.0.0", {"start": v(-2.5, 88.01) * mm, "end": v(-2.5, 51.81) * mm, "construction": true});
            skLineSegment(sketch, "E237.0.1", {"start": v(-2.5, 51.81) * mm, "end": v(2.5, 51.81) * mm, "construction": true});
            skLineSegment(sketch, "E237.0.2", {"start": v(2.5, 51.81) * mm, "end": v(2.5, 88.01) * mm, "construction": true});
            skLineSegment(sketch, "E237.0.3", {"start": v(2.5, 88.01) * mm, "end": v(-2.5, 88.01) * mm, "construction": true});
            skLineSegment(sketch, "E238.0.0", {"start": v(156.88, 46.65) * mm, "end": v(138.78, 15.3) * mm, "construction": true});
            skLineSegment(sketch, "E238.0.1", {"start": v(138.78, 15.3) * mm, "end": v(143.12, 12.8) * mm, "construction": true});
            skLineSegment(sketch, "E238.0.2", {"start": v(143.12, 12.8) * mm, "end": v(161.22, 44.15) * mm, "construction": true});
            skLineSegment(sketch, "E238.0.3", {"start": v(161.22, 44.15) * mm, "end": v(156.88, 46.65) * mm, "construction": true});
            skCircle(sketch, "E239", {"center": v(0, -230.09) * mm, "radius": 281.9 * mm, "construction": true});
            skCircle(sketch, "E240", {"center": v(0, -230.09) * mm, "radius": 318.1 * mm, "construction": true});
            skLineSegment(sketch, "E241", {"start": v(-2.5, 88.01) * mm, "end": v(2.5, 51.81) * mm, "construction": true});
            skPoint(sketch, "E242", {"position": v(0, 69.91) * mm});
            skLineSegment(sketch, "E243.0.2", {"start": v(-2.5, 51.81) * mm, "end": v(7.31, 86.66) * mm, "construction": true});
            skLineSegment(sketch, "E243.0.1", {"start": v(-7.31, 53.17) * mm, "end": v(-2.5, 51.81) * mm, "construction": true});
            skLineSegment(sketch, "E243.0.3", {"start": v(7.31, 86.66) * mm, "end": v(2.5, 88.01) * mm, "construction": true});
            skLineSegment(sketch, "E244", {"start": v(2.5, 88.01) * mm, "end": v(-2.5, 51.81) * mm, "construction": true});
            skLineSegment(sketch, "E243.0.0", {"start": v(2.5, 88.01) * mm, "end": v(-7.31, 53.17) * mm, "construction": true});
            skArc(sketch, "E245", {"start": v(7.27, 86.5) * mm, "mid": v(2.48, 87.84) * mm, "end": v(-2.5, 87.84) * mm, "construction": true});
            skArc(sketch, "E246.trimOffspring", {"start": v(-7.27, 53.34) * mm, "mid": v(-2.48, 51.98) * mm, "end": v(2.5, 51.99) * mm});
            skLineSegment(sketch, "E247", {"start": v(0, 69.91) * mm, "end": v(7.27, 86.5) * mm, "construction": true});
            skArc(sketch, "E248.trimOffspring", {"start": v(0, 69.91) * mm, "mid": v(11.92, 74.57) * mm, "end": v(7.27, 86.5) * mm});
            skLineSegment(sketch, "E249", {"start": v(0, 69.91) * mm, "end": v(-7.27, 53.34) * mm, "construction": true});
            skArc(sketch, "E250", {"start": v(0, 69.91) * mm, "mid": v(-11.92, 65.26) * mm, "end": v(-7.27, 53.34) * mm});
            skLineSegment(sketch, "E251", {"start": v(0, -230.09) * mm, "end": v(82.33, 77.17) * mm, "construction": true});
            skLineSegment(sketch, "E252", {"start": v(2.5, 88.01) * mm, "end": v(82.33, 77.17) * mm, "construction": true});
            skLineSegment(sketch, "E253", {"start": v(82.33, 77.17) * mm, "end": v(156.88, 46.65) * mm, "construction": true});
            skLineSegment(sketch, "E254", {"start": v(7.27, 86.5) * mm, "end": v(7.67, 87.92) * mm});
            skArc(sketch, "E255", {"start": v(82.33, 77.17) * mm, "mid": v(45.32, 84.77) * mm, "end": v(7.67, 87.92) * mm});
            skLineSegment(sketch, "E256", {"start": v(82.33, 77.17) * mm, "end": v(72.96, 42.2) * mm});
            skLineSegment(sketch, "E257", {"start": v(2.5, 51.99) * mm, "end": v(2.5, 51.8) * mm});
            skArc(sketch, "E258", {"start": v(72.96, 42.2) * mm, "mid": v(38.03, 49.24) * mm, "end": v(2.5, 51.8) * mm});
            skArc(sketch, "E259.2.0", {"start": v(150, 29.72) * mm, "mid": v(162.65, 27.8) * mm, "end": v(164.58, 40.44) * mm});
            skArc(sketch, "E259.2.1", {"start": v(164.58, 40.44) * mm, "mid": v(161.1, 44) * mm, "end": v(156.8, 46.5) * mm});
            skArc(sketch, "E259.2.2", {"start": v(150, 29.72) * mm, "mid": v(137.35, 31.65) * mm, "end": v(135.42, 19) * mm});
            skArc(sketch, "E259.2.3", {"start": v(135.42, 19) * mm, "mid": v(137.02, 17.1) * mm, "end": v(138.87, 15.45) * mm});
            skLineSegment(sketch, "E259.anchor1", {"start": v(0, -230.09) * mm, "end": v(0, 69.91) * mm, "construction": true});
            skLineSegment(sketch, "E259.anchor2", {"start": v(0, -230.09) * mm, "end": v(150, 29.72) * mm, "construction": true});
            skArc(sketch, "E260", {"start": v(138.87, 15.45) * mm, "mid": v(140.95, 14.05) * mm, "end": v(143.2, 12.95) * mm, "construction": true});
            skLineSegment(sketch, "E261", {"start": v(138.87, 15.45) * mm, "end": v(138.78, 15.29) * mm});
            skArc(sketch, "E262", {"start": v(138.78, 15.29) * mm, "mid": v(106.72, 30.83) * mm, "end": v(72.96, 42.2) * mm});
            skLineSegment(sketch, "E263", {"start": v(156.8, 46.5) * mm, "end": v(156.88, 46.64) * mm});
            skArc(sketch, "E264", {"start": v(156.88, 46.64) * mm, "mid": v(120.58, 64.28) * mm, "end": v(82.33, 77.17) * mm});
            skLineSegment(sketch, "E265", {"start": v(0, -230.09) * mm, "end": v(42.42, 82.6) * mm, "construction": true});
            skCircle(sketch, "E266", {"center": v(35.7, 66.53) * mm, "radius": 1 * mm});
            skLineSegment(sketch, "E267", {"start": v(38.67, 66.13) * mm, "end": v(35.7, 66.53) * mm, "construction": true});
            skLineSegment(sketch, "E268", {"start": v(41.64, 65.72) * mm, "end": v(44.61, 65.32) * mm, "construction": true});
            skLineSegment(sketch, "E269", {"start": v(38.67, 66.13) * mm, "end": v(41.64, 65.72) * mm, "construction": true});
            skPoint(sketch, "E270", {"position": v(40.15, 65.92) * mm});
            skCircle(sketch, "E271", {"center": v(38.67, 66.13) * mm, "radius": 1 * mm});
            skCircle(sketch, "E272", {"center": v(41.64, 65.72) * mm, "radius": 1 * mm});
            skCircle(sketch, "E273", {"center": v(44.61, 65.32) * mm, "radius": 1 * mm});
            skLineSegment(sketch, "E274", {"start": v(42.42, 82.6) * mm, "end": v(37.9, 49.25) * mm, "construction": true});
            skLineSegment(sketch, "E275.MirrorCS", {"start": v(114.62, 45.77) * mm, "end": v(111.84, 46.91) * mm});
            skPoint(sketch, "E276.MirrorP", {"position": v(113.23, 46.34) * mm});
            skCircle(sketch, "E277.MirrorC", {"center": v(111.84, 46.91) * mm, "radius": 1 * mm});
            skCircle(sketch, "E278.MirrorC", {"center": v(114.62, 45.77) * mm, "radius": 1 * mm});
            skLineSegment(sketch, "E279.MirrorCS", {"start": v(111.84, 46.91) * mm, "end": v(109.07, 48.05) * mm});
            skCircle(sketch, "E280.MirrorC", {"center": v(117.4, 44.64) * mm, "radius": 1 * mm});
            skCircle(sketch, "E281.MirrorC", {"center": v(109.07, 48.05) * mm, "radius": 1 * mm});
            skLineSegment(sketch, "E282.MirrorCS", {"start": v(114.62, 45.77) * mm, "end": v(117.4, 44.64) * mm});
            skCircle(sketch, "E283", {"center": v(-3.63, 61.62) * mm, "radius": 1 * mm});
            skCircle(sketch, "E284", {"center": v(157.3, 35.08) * mm, "radius": 1 * mm});
            skSolve(sketch);
        }
        {
            var Q0;
            Q0 = qSketchRegion(id + "F57", true);
            extrude(context, id + "F58", {"entities" : qUnion([Q0]), "endBound" : BoundingType.SYMMETRIC, "depth" : 5 * mm});
        }
        {
            var Q0;
            Q0=makeQuery(id+"F58.opExtrude","SWEPT_BODY",BODY,{"disambiguationData":[OSD([sQuery(id+"F57.wireOp",EDGE,"E246.trimOffspring"),sQuery(id+"F57.wireOp",EDGE,"E248.trimOffspring"),sQuery(id+"F57.wireOp",EDGE,"E250"),sQuery(id+"F57.wireOp",EDGE,"E254"),sQuery(id+"F57.wireOp",EDGE,"E255"),sQuery(id+"F57.wireOp",EDGE,"E257"),sQuery(id+"F57.wireOp",EDGE,"E258"),sQuery(id+"F57.wireOp",EDGE,"E259.2.0"),sQuery(id+"F57.wireOp",EDGE,"E259.2.1"),sQuery(id+"F57.wireOp",EDGE,"E259.2.2"),sQuery(id+"F57.wireOp",EDGE,"E259.2.3"),sQuery(id+"F57.wireOp",EDGE,"E261"),sQuery(id+"F57.wireOp",EDGE,"E262"),sQuery(id+"F57.wireOp",EDGE,"E263"),sQuery(id+"F57.wireOp",EDGE,"E264")])]});
            var Q1;
            Q1=sQuery(id+"F0.wireOp",EDGE,"E6");
            circularPattern(context, id + "F59", {"entities" : qUnion([Q0]), "axis" : qUnion([Q1]), "angle" : 360 * degree, "instanceCount" : 12, "equalSpace" : true});
        }
        {
            var Q0;
            Q0=qCreatedBy(id+"F44.planeOp",FACE);
            var sketch = newSketch(context, id + "F60", { "sketchPlane" : qUnion([Q0])});
            skPoint(sketch, "E285.0", {"position": v(0, -230.09) * mm});
            skLineSegment(sketch, "E286", {"start": v(0, -230.09) * mm, "end": v(15.53, -172.13) * mm, "construction": true});
            skCircle(sketch, "E287", {"center": v(0, -230.09) * mm, "radius": 60 * mm, "construction": true});
            skLineSegment(sketch, "E288", {"start": v(15.53, -172.13) * mm, "end": v(14.08, -171.74) * mm, "construction": true});
            skLineSegment(sketch, "E289", {"start": v(15.53, -172.13) * mm, "end": v(16.98, -172.52) * mm, "construction": true});
            skLineSegment(sketch, "E290", {"start": v(14.08, -171.74) * mm, "end": v(11.18, -170.97) * mm, "construction": true});
            skLineSegment(sketch, "E291", {"start": v(16.98, -172.52) * mm, "end": v(19.88, -173.3) * mm, "construction": true});
            skLineSegment(sketch, "E292", {"start": v(14.08, -171.74) * mm, "end": v(16.98, -172.52) * mm, "construction": true});
            skCircle(sketch, "E293", {"center": v(16.98, -172.52) * mm, "radius": 1 * mm});
            skCircle(sketch, "E294", {"center": v(19.88, -173.3) * mm, "radius": 1 * mm});
            skCircle(sketch, "E295", {"center": v(14.08, -171.74) * mm, "radius": 1 * mm});
            skCircle(sketch, "E296", {"center": v(11.18, -170.97) * mm, "radius": 1 * mm});
            skCircle(sketch, "E297.1.0", {"center": v(-45.6, -190.84) * mm, "radius": 1 * mm});
            skCircle(sketch, "E297.1.1", {"center": v(-43.49, -188.72) * mm, "radius": 1 * mm});
            skCircle(sketch, "E297.1.2", {"center": v(-41.37, -186.6) * mm, "radius": 1 * mm});
            skCircle(sketch, "E297.1.3", {"center": v(-39.24, -184.48) * mm, "radius": 1 * mm});
            skCircle(sketch, "E297.2.0", {"center": v(-56.8, -249.96) * mm, "radius": 1 * mm});
            skCircle(sketch, "E297.2.1", {"center": v(-57.57, -247.07) * mm, "radius": 1 * mm});
            skCircle(sketch, "E297.2.2", {"center": v(-58.34, -244.17) * mm, "radius": 1 * mm});
            skCircle(sketch, "E297.2.3", {"center": v(-59.12, -241.27) * mm, "radius": 1 * mm});
            skLineSegment(sketch, "E297.anchor1", {"start": v(0, -230.09) * mm, "end": v(11.18, -170.97) * mm, "construction": true});
            skLineSegment(sketch, "E297.anchor2", {"start": v(0, -230.09) * mm, "end": v(56.8, -210.21) * mm, "construction": true});
            skCircle(sketch, "E298.1.3.0", {"center": v(-11.18, -289.2) * mm, "radius": 1 * mm});
            skCircle(sketch, "E298.2.3.0", {"center": v(-14.08, -288.43) * mm, "radius": 1 * mm});
            skCircle(sketch, "E298.4.3.0", {"center": v(-16.98, -287.65) * mm, "radius": 1 * mm});
            skCircle(sketch, "E298.6.3.0", {"center": v(-19.88, -286.88) * mm, "radius": 1 * mm});
            skCircle(sketch, "E298.1.4.0", {"center": v(45.6, -269.33) * mm, "radius": 1 * mm});
            skCircle(sketch, "E298.2.4.0", {"center": v(43.49, -271.45) * mm, "radius": 1 * mm});
            skCircle(sketch, "E298.4.4.0", {"center": v(41.37, -273.57) * mm, "radius": 1 * mm});
            skCircle(sketch, "E298.6.4.0", {"center": v(39.24, -275.7) * mm, "radius": 1 * mm});
            skCircle(sketch, "E298.1.5.0", {"center": v(56.8, -210.21) * mm, "radius": 1 * mm});
            skCircle(sketch, "E298.2.5.0", {"center": v(57.57, -213.1) * mm, "radius": 1 * mm});
            skCircle(sketch, "E298.4.5.0", {"center": v(58.34, -216) * mm, "radius": 1 * mm});
            skCircle(sketch, "E298.6.5.0", {"center": v(59.12, -218.9) * mm, "radius": 1 * mm});
            skSolve(sketch);
        }
        {
            var Q0;
            Q0 = qSketchRegion(id + "F60", true);
            extrude(context, id + "F61", {"entities" : qUnion([Q0]), "operationType" : NewBodyOperationType.REMOVE, "endBound" : BoundingType.THROUGH_ALL, "oppositeDirection" : true, "depth" : 25 * mm});
        }
        {
            var Q0;
            Q0=makeQuery(id+"F7.opPattern","COPY",FACE,{"derivedFrom":makeQuery(id+"F5.opExtrude","SWEPT_FACE",FACE,{"disambiguationData":[OSD([sQuery(id+"F4.wireOp",EDGE,"E24.top")])]}),"instanceName":"1"});
            var sketch = newSketch(context, id + "F62", { "sketchPlane" : qUnion([Q0])});
            skPoint(sketch, "E299.0", {"position": v(-42, 42) * mm});
            skPoint(sketch, "E300.0", {"position": v(42, -42) * mm});
            skLineSegment(sketch, "E301", {"start": v(-42, 42) * mm, "end": v(42, -42) * mm, "construction": true});
            skLineSegment(sketch, "E302", {"start": v(0, 0) * mm, "end": v(0, -100.86) * mm, "construction": true});
            skLineSegment(sketch, "E303", {"start": v(0, 0) * mm, "end": v(105.24, 0) * mm, "construction": true});
            skSolve(sketch);
        }
        {
            var Q0;
            Q0=makeQuery(id+"F5.opExtrude","SWEPT_BODY",BODY,{"disambiguationData":[OSD([sQuery(id+"F4.wireOp",EDGE,"E17"),sQuery(id+"F4.wireOp",EDGE,"E19"),sQuery(id+"F4.wireOp",EDGE,"E20"),sQuery(id+"F4.wireOp",EDGE,"E21"),sQuery(id+"F4.wireOp",EDGE,"E22"),sQuery(id+"F4.wireOp",EDGE,"E23"),sQuery(id+"F4.wireOp",EDGE,"E24.top"),sQuery(id+"F4.wireOp",EDGE,"E24.left"),sQuery(id+"F4.wireOp",EDGE,"E24.right"),sQuery(id+"F4.wireOp",EDGE,"E25.top"),sQuery(id+"F4.wireOp",EDGE,"E25.left"),sQuery(id+"F4.wireOp",EDGE,"E25.right"),sQuery(id+"F4.wireOp",EDGE,"E26.trimOffspring"),sQuery(id+"F4.wireOp",EDGE,"E27.trimOffspring")])]});
            var Q1;
            Q1=makeQuery(id+"F7.opPattern","COPY",BODY,{"derivedFrom":makeQuery(id+"F5.opExtrude","SWEPT_BODY",BODY,{"disambiguationData":[OSD([sQuery(id+"F4.wireOp",EDGE,"E17"),sQuery(id+"F4.wireOp",EDGE,"E19"),sQuery(id+"F4.wireOp",EDGE,"E20"),sQuery(id+"F4.wireOp",EDGE,"E21"),sQuery(id+"F4.wireOp",EDGE,"E22"),sQuery(id+"F4.wireOp",EDGE,"E23"),sQuery(id+"F4.wireOp",EDGE,"E24.top"),sQuery(id+"F4.wireOp",EDGE,"E24.left"),sQuery(id+"F4.wireOp",EDGE,"E24.right"),sQuery(id+"F4.wireOp",EDGE,"E25.top"),sQuery(id+"F4.wireOp",EDGE,"E25.left"),sQuery(id+"F4.wireOp",EDGE,"E25.right"),sQuery(id+"F4.wireOp",EDGE,"E26.trimOffspring"),sQuery(id+"F4.wireOp",EDGE,"E27.trimOffspring")])]}),"instanceName":"1"});
            var Q2;
            Q2=sQuery(id+"F62.wireOp",EDGE,"E302");
            transform(context, id + "F63", {"entities" : qUnion([Q0, Q1]), "transformType" : TransformType.ROTATION, "transformAxis" : qUnion([Q2]), "angle" : 180 * degree, "makeCopy" : false});
        }
        {
            var Q0;
            Q0=makeQuery(id+"F9.opExtrude","SWEPT_BODY",BODY,{"disambiguationData":[OSD([sQuery(id+"F8.wireOp",EDGE,"E31"),sQuery(id+"F8.wireOp",EDGE,"E32"),sQuery(id+"F8.wireOp",EDGE,"E33"),sQuery(id+"F8.wireOp",EDGE,"E34"),sQuery(id+"F8.wireOp",EDGE,"E35"),sQuery(id+"F8.wireOp",EDGE,"E38"),sQuery(id+"F8.wireOp",EDGE,"E39"),sQuery(id+"F8.wireOp",EDGE,"E40"),sQuery(id+"F8.wireOp",EDGE,"E41"),sQuery(id+"F8.wireOp",EDGE,"E42"),sQuery(id+"F8.wireOp",EDGE,"E43"),sQuery(id+"F8.wireOp",EDGE,"E44"),sQuery(id+"F8.wireOp",EDGE,"E45.trimOffspring"),sQuery(id+"F8.wireOp",EDGE,"E46.trimOffspring")])]});
            var Q1;
            Q1=makeQuery(id+"F11.opPattern","COPY",BODY,{"derivedFrom":makeQuery(id+"F9.opExtrude","SWEPT_BODY",BODY,{"disambiguationData":[OSD([sQuery(id+"F8.wireOp",EDGE,"E31"),sQuery(id+"F8.wireOp",EDGE,"E32"),sQuery(id+"F8.wireOp",EDGE,"E33"),sQuery(id+"F8.wireOp",EDGE,"E34"),sQuery(id+"F8.wireOp",EDGE,"E35"),sQuery(id+"F8.wireOp",EDGE,"E38"),sQuery(id+"F8.wireOp",EDGE,"E39"),sQuery(id+"F8.wireOp",EDGE,"E40"),sQuery(id+"F8.wireOp",EDGE,"E41"),sQuery(id+"F8.wireOp",EDGE,"E42"),sQuery(id+"F8.wireOp",EDGE,"E43"),sQuery(id+"F8.wireOp",EDGE,"E44"),sQuery(id+"F8.wireOp",EDGE,"E45.trimOffspring"),sQuery(id+"F8.wireOp",EDGE,"E46.trimOffspring")])]}),"instanceName":"1"});
            var Q2;
            Q2=sQuery(id+"F62.wireOp",EDGE,"E303");
            transform(context, id + "F64", {"entities" : qUnion([Q0, Q1]), "transformType" : TransformType.ROTATION, "transformAxis" : qUnion([Q2]), "angle" : 180 * degree, "makeCopy" : false});
        }
    });
